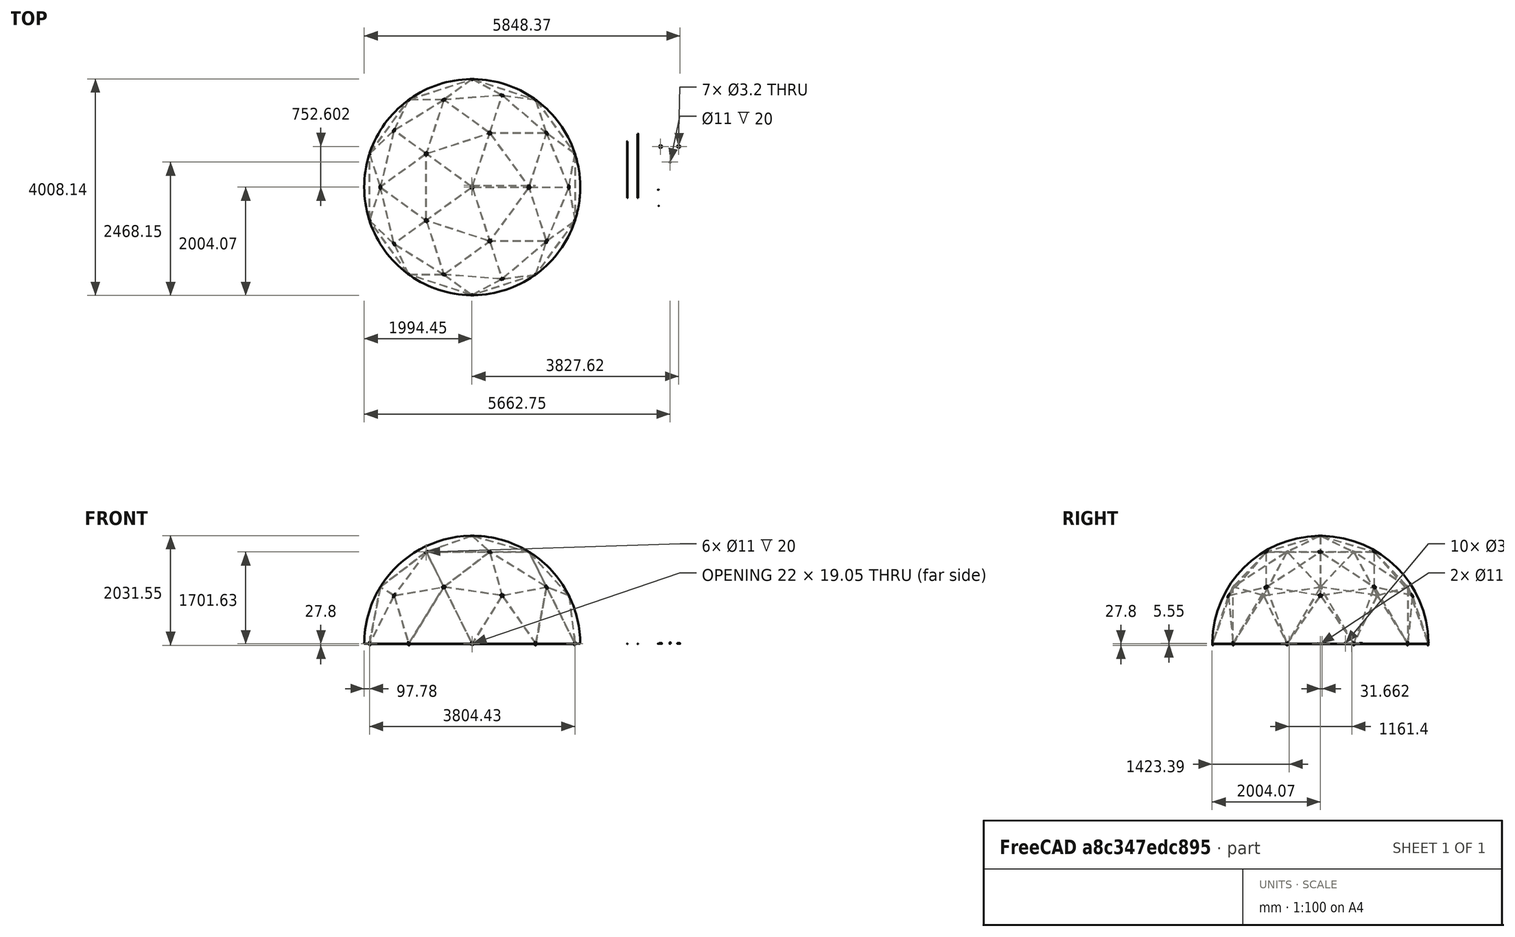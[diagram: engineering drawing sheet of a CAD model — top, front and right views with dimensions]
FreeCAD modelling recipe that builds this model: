
FCSTD DOCUMENT  (FreeCAD 0.16R6707 (Git))
Label: domo-3D
License: All rights reserved
LicenseURL: http://en.wikipedia.org/wiki/All_rights_reserved
objects: Part::Feature×235, Part::Part2DObjectPython×141, App::DocumentObjectGroup×21, App::Annotation×18, Part::Mirroring×7, App::FeaturePython×4, Part::Sphere×1, Part::Cylinder×1
note: 385 computed .brp shape members not serialized (recipe doc carries the construction recipe); baked Part::Feature solids carry a one-line shape summary decoded from their .brp

FEATURE [Part::Part2DObjectPython] Line  # Draft 2D object (typed FeaturePython)
  ChamferSize = 0
  Closed = false
  End = (-1902.16,617.998,0)
  FilletRadius = 0
  Length = 1236.1
  MakeFace = true
  Placement = pos=(-1154.86,1595.54,0) rot=(0,0,-1;0.628319rad)
  Points = (2) [(-30,6,0),(-30,-1230.1,0)]
  Start = (-1175.6,1618.02,0)
  Subdivisions = 0
FEATURE [Part::Part2DObjectPython] Line003  # Draft 2D object (typed FeaturePython)
  ChamferSize = 0
  Closed = false
  End = (-1175.6,1618.02,0)
  FilletRadius = 0
  Length = 1236.1
  MakeFace = true
  Placement = pos=(3.56417,1969.61,0) rot=(0,0,-1;1.25664rad)
  Points = (2) [(-30,6,0),(-30,-1230.1,0)]
  Start = (3.6e-11,2000,0)
  Subdivisions = 0
FEATURE [Part::Mirroring] Part__Mirroring  label="Line (Mirror #1)"
  Base = (0,0,0)
  Normal = (1,0,0)
  Source = -> Line
FEATURE [Part::Mirroring] Part__Mirroring001  label="Line003 (Mirror #2)"
  Base = (0,0,0)
  Normal = (1,0,0)
  Source = -> Line003
FEATURE [Part::Mirroring] Part__Mirroring002  label="Line (Mirror #3)"
  Base = (0,0,0)
  Normal = (0,1,0)
  Source = -> Line
FEATURE [Part::Mirroring] Part__Mirroring003  label="Line003 (Mirror #4)"
  Base = (0,0,0)
  Normal = (0,1,0)
  Source = -> Line003
FEATURE [Part::Mirroring] Part__Mirroring004  label="Line (Mirror #5)"
  Base = (0,0,0)
  Normal = (0,1,0)
  Source = -> Part__Mirroring
FEATURE [Part::Mirroring] Part__Mirroring005  label="Line003 (Mirror #6)"
  Base = (0,0,0)
  Normal = (0,1,0)
  Source = -> Part__Mirroring001
FEATURE [Part::Part2DObjectPython] Line006  # Draft 2D object (typed FeaturePython)
  ChamferSize = 0
  Closed = false
  End = (-1902.16,-617.998,0)
  FilletRadius = 0
  Length = 1236
  MakeFace = true
  Points = (2) [(-1902.16,617.998,0),(-1902.16,-617.998,0)]
  Start = (-1902.16,617.998,0)
  Subdivisions = 0
FEATURE [Part::Sphere] Sphere
  Angle1 = 0
  Angle2 = 90
  Angle3 = 360
  Radius = 2000
FEATURE [Part::Part2DObjectPython] Line014  # Draft 2D object (typed FeaturePython)
  ChamferSize = 0
  Closed = false
  End = (1902.16,3e-10,0)
  FilletRadius = 0
  Length = 1902.16
  MakeFace = true
  Points = (2) [(-1.99975e-10,3.00133e-10,0),(1902.16,3.0025e-10,0)]
  Start = (0,0,0)
  Subdivisions = 0
FEATURE [Part::Part2DObjectPython] Line015  # Draft 2D object (typed FeaturePython)
  ChamferSize = 0
  Closed = false
  End = (1902.16,3e-10,0)
  FilletRadius = 0
  Length = 1902.16
  MakeFace = true
  Points = (2) [(-1.99975e-10,3.00133e-10,0),(1902.16,3.0025e-10,0)]
  Start = (0,0,0)
  Subdivisions = 0
FEATURE [Part::Part2DObjectPython] Line016  # Draft 2D object (typed FeaturePython)
  ChamferSize = 0
  Closed = false
  End = (587.785,1809.02,0)
  FilletRadius = 0
  Length = 1902.11
  MakeFace = true
  Points = (2) [(-1.99975e-10,3.00133e-10,0),(587.785,1809.02,0)]
  Start = (0,0,0)
  Subdivisions = 0
FEATURE [Part::Part2DObjectPython] Line017  # Draft 2D object (typed FeaturePython)
  ChamferSize = 0
  Closed = false
  End = (-1538.86,1118.05,0)
  FilletRadius = 0
  Length = 1902.13
  MakeFace = true
  Points = (2) [(-1.99975e-10,3.00133e-10,0),(-1538.86,1118.05,0)]
  Start = (0,0,0)
  Subdivisions = 0
FEATURE [Part::Part2DObjectPython] Line018  # Draft 2D object (typed FeaturePython)
  ChamferSize = 0
  Closed = false
  End = (-1538.86,-1118.05,0)
  FilletRadius = 0
  Length = 1902.13
  MakeFace = true
  Points = (2) [(-1.99975e-10,3.00133e-10,0),(-1538.86,-1118.05,0)]
  Start = (0,0,0)
  Subdivisions = 0
FEATURE [Part::Part2DObjectPython] Line019  # Draft 2D object (typed FeaturePython)
  ChamferSize = 0
  Closed = false
  End = (-577.454,-703.099,0)
  FilletRadius = 0
  Length = 1093.1
  MakeFace = true
  Placement = pos=(1075.61,-2380.95,0) rot=(0,0,-1;0.581932rad)
  Points = (2) [(-2300,-600,0),(-2303.19,493.095,0)]
  Start = (-1175.6,-1618.02,0)
  Subdivisions = 0
FEATURE [Part::Part2DObjectPython] Line022  # Draft 2D object (typed FeaturePython)
  ChamferSize = 0
  Closed = false
  End = (587.8,-1809.01,0)
  FilletRadius = 0
  Length = 1902.11
  MakeFace = true
  Points = (2) [(-1.99975e-10,3.00133e-10,0),(587.8,-1809.01,0)]
  Start = (0,0,0)
  Subdivisions = 0
FEATURE [Part::Part2DObjectPython] Line023  # Draft 2D object (typed FeaturePython)
  ChamferSize = 0
  Closed = false
  End = (0,0,2000)
  FilletRadius = 0
  Length = 2000
  MakeFace = true
  Points = (2) [(-1.99975e-10,3.00133e-10,0),(1.22465e-13,-2.99952e-29,2000)]
  Start = (0,0,0)
  Subdivisions = 0
FEATURE [Part::Part2DObjectPython] DWire001  # Draft 2D object (typed FeaturePython)
  ChamferSize = 0
  Closed = true
  End = (1902.16,617.998,0)
  FilletRadius = 0
  Length = 3422.2
  MakeFace = true
  Points = (3) [(1902.16,-617.998,0),(1788.83,-9.64734e-10,894.484),(1902.16,617.998,0)]
  Start = (1902.16,-617.998,0)
  Subdivisions = 0
FEATURE [Part::Part2DObjectPython] DWire  # Draft 2D object (typed FeaturePython)
  ChamferSize = 0
  Closed = true
  End = (587.785,1809.02,0)
  FilletRadius = 0
  Length = 6662.19
  MakeFace = true
  Points = (3) [(1.22465e-13,0,2000),(-1.99975e-10,3.00133e-10,0),(587.785,1809.02,0)]
  Start = (0,0,2000)
  Subdivisions = 0
FEATURE [Part::Mirroring] Part__Mirroring006  label="DWire003 (Mirror #7)"
  Base = (0,0,0)
  Normal = (0,1,0)
FEATURE [Part::Part2DObjectPython] Arc  # Draft 2D object (typed FeaturePython)
  FirstAngle = 56.8247
  LastAngle = 105.817
  MakeFace = true
  Placement = pos=(-1175.6,-1618.02,0) rot=(0,0,1;0rad)
  Radius = 1093.1
FEATURE [Part::Part2DObjectPython] Line026  # Draft 2D object (typed FeaturePython)
  ChamferSize = 0
  Closed = false
  End = (-1902.16,-617.998,0)
  FilletRadius = 0
  Length = 1093.15
  MakeFace = true
  Points = (2) [(-809.424,-588.081,0),(-1902.16,-617.998,0)]
  Start = (-809.424,-588.081,0)
  Subdivisions = 0
FEATURE [Part::Part2DObjectPython] DWire004  # Draft 2D object (typed FeaturePython)
  ChamferSize = 0
  Closed = true
  End = (-1538.86,-1118.05,0)
  FilletRadius = 0
  Length = 6662.22
  MakeFace = true
  Points = (3) [(1.22465e-13,0,2000),(-1.99975e-10,3.00133e-10,0),(-1538.86,-1118.05,0)]
  Start = (0,0,2000)
  Subdivisions = 0
FEATURE [Part::Part2DObjectPython] DWire005  # Draft 2D object (typed FeaturePython)
  ChamferSize = 0
  Closed = true
  End = (-1175.6,-1618.02,0)
  FilletRadius = 0
  Length = 3422.35
  MakeFace = true
  Points = (3) [(-1902.16,-617.998,0),(-1447.19,-1051.45,894.481),(-1175.6,-1618.02,0)]
  Start = (-1902.16,-617.998,0)
  Subdivisions = 0
FEATURE [Part::Part2DObjectPython] Line027  # Draft 2D object (typed FeaturePython)
  ChamferSize = 0
  Closed = false
  End = (-878.683,234.127,0)
  FilletRadius = 0
  Length = 1093.1
  MakeFace = true
  Placement = pos=(-2154.97,-1745.49,0) rot=(0,0,-1;1.93254rad)
  Points = (2) [(-2300,-600,0),(-2303.19,493.095,0)]
  Start = (-1902.16,617.998,0)
  Subdivisions = 0
FEATURE [Part::Part2DObjectPython] Arc003  # Draft 2D object (typed FeaturePython)
  FirstAngle = -20.5593
  LastAngle = 28.7005
  MakeFace = true
  Placement = pos=(-1902.16,617.998,0) rot=(0,0,1;0rad)
  Radius = 1093.1
FEATURE [Part::Part2DObjectPython] DWire006  # Draft 2D object (typed FeaturePython)
  ChamferSize = 0
  Closed = true
  End = (-1538.86,1118.05,0)
  FilletRadius = 0
  Length = 6662.22
  MakeFace = true
  Points = (3) [(1.22465e-13,0,2000),(-1.99975e-10,3.00133e-10,0),(-1538.86,1118.05,0)]
  Start = (0,0,2000)
  Subdivisions = 0
FEATURE [Part::Part2DObjectPython] DWire007  # Draft 2D object (typed FeaturePython)
  ChamferSize = 0
  Closed = true
  End = (-1902.16,617.998,0)
  FilletRadius = 0
  Length = 3422.25
  MakeFace = true
  Points = (3) [(-1175.6,1618.02,0),(-1447.21,1051.46,894.426),(-1902.16,617.998,0)]
  Start = (-1175.6,1618.02,0)
  Subdivisions = 0
FEATURE [Part::Part2DObjectPython] DWire008  # Draft 2D object (typed FeaturePython)
  ChamferSize = 0
  Closed = true
  End = (324.937,-1000.03,1701.28)
  FilletRadius = 0
  Length = 3422.31
  MakeFace = true
  Points = (3) [(2.23523e-10,2.82703e-10,2000),(-850.675,-618.052,1701.28),(324.937,-1000.03,1701.28)]
  Start = (2.24e-10,2.83e-10,2000)
  Subdivisions = 0
FEATURE [Part::Part2DObjectPython] DWire009  # Draft 2D object (typed FeaturePython)
  ChamferSize = 0
  Closed = true
  End = (-2e-10,3e-10,2000)
  FilletRadius = 0
  Length = 3422.3
  MakeFace = true
  Points = (3) [(324.937,-1000.03,1701.28),(1051.49,1.3321e-09,1701.28),(-1.99876e-10,3.00061e-10,2000)]
  Start = (324.937,-1000.03,1701.28)
  Subdivisions = 0
FEATURE [Part::Part2DObjectPython] DWire010  # Draft 2D object (typed FeaturePython)
  ChamferSize = 0
  Closed = true
  End = (324.929,1000.03,1701.28)
  FilletRadius = 0
  Length = 3422.3
  MakeFace = true
  Points = (3) [(-1.99876e-10,3.00061e-10,2000),(1051.49,1.3321e-09,1701.28),(324.929,1000.03,1701.28)]
  Start = (-2e-10,3e-10,2000)
  Subdivisions = 0
FEATURE [Part::Part2DObjectPython] DWire011  # Draft 2D object (typed FeaturePython)
  ChamferSize = 0
  Closed = true
  End = (-850.675,618.052,1701.28)
  FilletRadius = 0
  Length = 3422.3
  MakeFace = true
  Points = (3) [(-1.99876e-10,3.00061e-10,2000),(324.929,1000.03,1701.28),(-850.675,618.052,1701.28)]
  Start = (-2e-10,3e-10,2000)
  Subdivisions = 0
FEATURE [Part::Part2DObjectPython] DWire012  # Draft 2D object (typed FeaturePython)
  ChamferSize = 0
  Closed = true
  End = (-850.675,-618.052,1701.28)
  FilletRadius = 0
  Length = 3422.3
  MakeFace = true
  Points = (3) [(-1.99876e-10,3.00061e-10,2000),(-850.675,618.052,1701.28),(-850.675,-618.052,1701.28)]
  Start = (-2e-10,3e-10,2000)
  Subdivisions = 0
FEATURE [Part::Part2DObjectPython] Line040  # Draft 2D object (typed FeaturePython)
  ChamferSize = 0
  Closed = false
  End = (-1447.19,-1051.45,894.481)
  FilletRadius = 0
  Length = 1092.97
  MakeFace = true
  Points = (2) [(-850.675,-618.052,1701.28),(-1447.19,-1051.45,894.481)]
  Start = (-850.675,-618.052,1701.28)
  Subdivisions = 0
FEATURE [Part::Part2DObjectPython] DWire013  # Draft 2D object (typed FeaturePython)
  ChamferSize = 0
  Closed = true
  End = (0,0,2000)
  FilletRadius = 0
  Length = 6662.22
  MakeFace = true
  Points = (3) [(1538.88,-1118.01,0),(-1.99975e-10,3.00133e-10,0),(1.22465e-13,0,2000)]
  Start = (1538.88,-1118.01,0)
  Subdivisions = 0
FEATURE [Part::Part2DObjectPython] Arc007  # Draft 2D object (typed FeaturePython)
  FirstAngle = -90
  LastAngle = 6.05971
  MakeFace = true
  Placement = pos=(-2e-10,3e-10,0) rot=(-0.908667,0.295233,-0.295233;1.66643rad)
  Radius = 2000
  Support = -> DWire013
FEATURE [Part::Part2DObjectPython] DWire014  # Draft 2D object (typed FeaturePython)
  ChamferSize = 0
  Closed = true
  End = (1902.16,-617.998,0)
  FilletRadius = 0
  Length = 3708.32
  MakeFace = true
  Points = (3) [(1175.6,-1618.02,0),(1376.39,-999.957,1051.5),(1902.16,-617.998,0)]
  Start = (1175.6,-1618.02,0)
  Subdivisions = 0
FEATURE [Part::Part2DObjectPython] DWire015  # Draft 2D object (typed FeaturePython)
  ChamferSize = 0
  Closed = true
  End = (1051.49,1.332e-09,1701.28)
  FilletRadius = 0
  Length = 3708.12
  MakeFace = true
  Points = (3) [(1376.39,-999.957,1051.5),(324.937,-1000.03,1701.28),(1051.49,1.3321e-09,1701.28)]
  Start = (1376.39,-999.957,1051.5)
  Subdivisions = 0
FEATURE [Part::Part2DObjectPython] DWire016  # Draft 2D object (typed FeaturePython)
  ChamferSize = 0
  Closed = true
  End = (1175.6,-1618.02,0)
  FilletRadius = 0
  Length = 3422.29
  MakeFace = true
  Points = (3) [(552.796,-1701.28,894.456),(1376.39,-999.957,1051.5),(1175.6,-1618.02,0)]
  Start = (552.796,-1701.28,894.456)
  Subdivisions = 0
FEATURE [Part::Part2DObjectPython] DWire017  # Draft 2D object (typed FeaturePython)
  ChamferSize = 0
  Closed = true
  End = (1902.16,-617.998,0)
  FilletRadius = 0
  Length = 3422.23
  MakeFace = true
  Points = (3) [(1376.39,-999.957,1051.5),(1788.83,-9.64734e-10,894.484),(1902.16,-617.998,0)]
  Start = (1376.39,-999.957,1051.5)
  Subdivisions = 0
FEATURE [Part::Part2DObjectPython] DWire018  # Draft 2D object (typed FeaturePython)
  ChamferSize = 0
  Closed = true
  End = (1376.39,-999.957,1051.5)
  FilletRadius = 0
  Length = 3422.11
  MakeFace = true
  Points = (3) [(324.937,-1000.03,1701.28),(552.796,-1701.28,894.456),(1376.39,-999.957,1051.5)]
  Start = (324.937,-1000.03,1701.28)
  Subdivisions = 0
FEATURE [Part::Part2DObjectPython] DWire019  # Draft 2D object (typed FeaturePython)
  ChamferSize = 0
  Closed = true
  End = (1788.83,-9.65e-10,894.484)
  FilletRadius = 0
  Length = 3421.98
  MakeFace = true
  Points = (3) [(1376.39,-999.957,1051.5),(1051.49,1.3321e-09,1701.28),(1788.83,-9.64734e-10,894.484)]
  Start = (1376.39,-999.957,1051.5)
  Subdivisions = 0
FEATURE [Part::Part2DObjectPython] DWire020  # Draft 2D object (typed FeaturePython)
  ChamferSize = 0
  Closed = true
  End = (1175.6,1618.02,0)
  FilletRadius = 0
  Length = 3708.32
  MakeFace = true
  Points = (3) [(1902.16,617.998,0),(1376.39,999.957,1051.5),(1175.6,1618.02,0)]
  Start = (1902.16,617.998,0)
  Subdivisions = 0
FEATURE [Part::Part2DObjectPython] DWire021  # Draft 2D object (typed FeaturePython)
  ChamferSize = 0
  Closed = true
  End = (-1175.6,1618.02,0)
  FilletRadius = 0
  Length = 3708.32
  MakeFace = true
  Points = (3) [(-525.738,1618.01,1051.5),(3.56977e-11,2000,0),(-1175.6,1618.02,0)]
  Start = (-525.738,1618.01,1051.5)
  Subdivisions = 0
FEATURE [Part::Part2DObjectPython] DWire022  # Draft 2D object (typed FeaturePython)
  ChamferSize = 0
  Closed = true
  End = (-1902.16,-617.998,0)
  FilletRadius = 0
  Length = 3708.18
  MakeFace = true
  Points = (3) [(-1701.28,-1.02242e-09,1051.5),(-1902.16,617.998,0),(-1902.16,-617.998,0)]
  Start = (-1701.28,-1.022e-09,1051.5)
  Subdivisions = 0
FEATURE [Part::Part2DObjectPython] DWire023  # Draft 2D object (typed FeaturePython)
  ChamferSize = 0
  Closed = true
  End = (-3.6e-11,-2000,0)
  FilletRadius = 0
  Length = 3708.32
  MakeFace = true
  Points = (3) [(-525.738,-1618.01,1051.5),(-1175.6,-1618.02,0),(-3.5925e-11,-2000,0)]
  Start = (-525.738,-1618.01,1051.5)
  Subdivisions = 0
FEATURE [Part::Part2DObjectPython] DWire024  # Draft 2D object (typed FeaturePython)
  ChamferSize = 0
  Closed = true
  End = (324.929,1000.03,1701.28)
  FilletRadius = 0
  Length = 3708.14
  MakeFace = true
  Points = (3) [(1051.49,1.3321e-09,1701.28),(1376.39,999.957,1051.5),(324.929,1000.03,1701.28)]
  Start = (1051.49,1.332e-09,1701.28)
  Subdivisions = 0
FEATURE [Part::Part2DObjectPython] DWire025  # Draft 2D object (typed FeaturePython)
  ChamferSize = 0
  Closed = true
  End = (1376.39,999.957,1051.5)
  FilletRadius = 0
  Length = 3421.98
  MakeFace = true
  Points = (3) [(1051.49,1.3321e-09,1701.28),(1788.83,-9.64734e-10,894.484),(1376.39,999.957,1051.5)]
  Start = (1051.49,1.332e-09,1701.28)
  Subdivisions = 0
FEATURE [Part::Part2DObjectPython] DWire026  # Draft 2D object (typed FeaturePython)
  ChamferSize = 0
  Closed = true
  End = (1376.39,999.957,1051.5)
  FilletRadius = 0
  Length = 3422.23
  MakeFace = true
  Points = (3) [(1788.83,-9.64734e-10,894.484),(1902.16,617.998,0),(1376.39,999.957,1051.5)]
  Start = (1788.83,-9.65e-10,894.484)
  Subdivisions = 0
FEATURE [Part::Part2DObjectPython] DWire027  # Draft 2D object (typed FeaturePython)
  ChamferSize = 0
  Closed = true
  End = (552.796,1701.28,894.456)
  FilletRadius = 0
  Length = 3422.29
  MakeFace = true
  Points = (3) [(1376.39,999.957,1051.5),(1175.6,1618.02,0),(552.796,1701.28,894.456)]
  Start = (1376.39,999.957,1051.5)
  Subdivisions = 0
FEATURE [Part::Part2DObjectPython] DWire028  # Draft 2D object (typed FeaturePython)
  ChamferSize = 0
  Closed = true
  End = (552.796,1701.28,894.456)
  FilletRadius = 0
  Length = 3422.12
  MakeFace = true
  Points = (3) [(324.929,1000.03,1701.28),(1376.39,999.957,1051.5),(552.796,1701.28,894.456)]
  Start = (324.929,1000.03,1701.28)
  Subdivisions = 0
FEATURE [Part::Part2DObjectPython] DWire029  # Draft 2D object (typed FeaturePython)
  ChamferSize = 0
  Closed = true
  End = (-3.6e-11,2000,0)
  FilletRadius = 0
  Length = 3422.29
  MakeFace = true
  Points = (3) [(-525.738,1618.01,1051.5),(552.796,1701.28,894.456),(-3.5925e-11,2000,0)]
  Start = (-525.738,1618.01,1051.5)
  Subdivisions = 0
FEATURE [Part::Part2DObjectPython] DWire030  # Draft 2D object (typed FeaturePython)
  ChamferSize = 0
  Closed = true
  End = (-525.738,1618.01,1051.5)
  FilletRadius = 0
  Length = 3422.11
  MakeFace = true
  Points = (3) [(324.929,1000.03,1701.28),(552.796,1701.28,894.456),(-525.738,1618.01,1051.5)]
  Start = (324.929,1000.03,1701.28)
  Subdivisions = 0
FEATURE [Part::Part2DObjectPython] DWire031  # Draft 2D object (typed FeaturePython)
  ChamferSize = 0
  Closed = true
  End = (-850.675,618.052,1701.28)
  FilletRadius = 0
  Length = 3708.14
  MakeFace = true
  Points = (3) [(324.929,1000.03,1701.28),(-525.738,1618.01,1051.5),(-850.675,618.052,1701.28)]
  Start = (324.929,1000.03,1701.28)
  Subdivisions = 0
FEATURE [Part::Part2DObjectPython] DWire032  # Draft 2D object (typed FeaturePython)
  ChamferSize = 0
  Closed = true
  End = (-1447.21,1051.46,894.426)
  FilletRadius = 0
  Length = 3422.21
  MakeFace = true
  Points = (3) [(-525.738,1618.01,1051.5),(-1175.6,1618.02,0),(-1447.21,1051.46,894.426)]
  Start = (-525.738,1618.01,1051.5)
  Subdivisions = 0
FEATURE [Part::Part2DObjectPython] DWire033  # Draft 2D object (typed FeaturePython)
  ChamferSize = 0
  Closed = true
  End = (-1447.21,1051.46,894.426)
  FilletRadius = 0
  Length = 3422.1
  MakeFace = true
  Points = (3) [(-525.738,1618.01,1051.5),(-850.675,618.052,1701.28),(-1447.21,1051.46,894.426)]
  Start = (-525.738,1618.01,1051.5)
  Subdivisions = 0
FEATURE [Part::Part2DObjectPython] DWire034  # Draft 2D object (typed FeaturePython)
  ChamferSize = 0
  Closed = true
  End = (-1701.28,-1.022e-09,1051.5)
  FilletRadius = 0
  Length = 3422.12
  MakeFace = true
  Points = (3) [(-850.675,618.052,1701.28),(-1447.21,1051.46,894.426),(-1701.28,-1.02242e-09,1051.5)]
  Start = (-850.675,618.052,1701.28)
  Subdivisions = 0
FEATURE [Part::Part2DObjectPython] DWire035  # Draft 2D object (typed FeaturePython)
  ChamferSize = 0
  Closed = true
  End = (-1701.28,-1.022e-09,1051.5)
  FilletRadius = 0
  Length = 3422.26
  MakeFace = true
  Points = (3) [(-1447.21,1051.46,894.426),(-1902.16,617.998,0),(-1701.28,-1.02242e-09,1051.5)]
  Start = (-1447.21,1051.46,894.426)
  Subdivisions = 0
FEATURE [Part::Part2DObjectPython] DWire036  # Draft 2D object (typed FeaturePython)
  ChamferSize = 0
  Closed = true
  End = (-850.675,-618.052,1701.28)
  FilletRadius = 0
  Length = 3708.14
  MakeFace = true
  Points = (3) [(-850.675,618.052,1701.28),(-1701.28,-1.02242e-09,1051.5),(-850.675,-618.052,1701.28)]
  Start = (-850.675,618.052,1701.28)
  Subdivisions = 0
FEATURE [Part::Part2DObjectPython] DWire037  # Draft 2D object (typed FeaturePython)
  ChamferSize = 0
  Closed = true
  End = (-1447.19,-1051.45,894.481)
  FilletRadius = 0
  Length = 3422.04
  MakeFace = true
  Points = (3) [(-1701.28,-1.02242e-09,1051.5),(-850.675,-618.052,1701.28),(-1447.19,-1051.45,894.481)]
  Start = (-1701.28,-1.022e-09,1051.5)
  Subdivisions = 0
FEATURE [Part::Part2DObjectPython] DWire038  # Draft 2D object (typed FeaturePython)
  ChamferSize = 0
  Closed = true
  End = (-1447.19,-1051.45,894.481)
  FilletRadius = 0
  Length = 3422.29
  MakeFace = true
  Points = (3) [(-1701.28,-1.02242e-09,1051.5),(-1902.16,-617.998,0),(-1447.19,-1051.45,894.481)]
  Start = (-1701.28,-1.022e-09,1051.5)
  Subdivisions = 0
FEATURE [Part::Part2DObjectPython] DWire039  # Draft 2D object (typed FeaturePython)
  ChamferSize = 0
  Closed = true
  End = (-525.738,-1618.01,1051.5)
  FilletRadius = 0
  Length = 3422.02
  MakeFace = true
  Points = (3) [(-850.675,-618.052,1701.28),(-1447.19,-1051.45,894.481),(-525.738,-1618.01,1051.5)]
  Start = (-850.675,-618.052,1701.28)
  Subdivisions = 0
FEATURE [Part::Part2DObjectPython] DWire040  # Draft 2D object (typed FeaturePython)
  ChamferSize = 0
  Closed = true
  End = (324.937,-1000.03,1701.28)
  FilletRadius = 0
  Length = 3708.15
  MakeFace = true
  Points = (3) [(-850.675,-618.052,1701.28),(-525.738,-1618.01,1051.5),(324.937,-1000.03,1701.28)]
  Start = (-850.675,-618.052,1701.28)
  Subdivisions = 0
FEATURE [Part::Part2DObjectPython] DWire041  # Draft 2D object (typed FeaturePython)
  ChamferSize = 0
  Closed = true
  End = (-1447.19,-1051.45,894.481)
  FilletRadius = 0
  Length = 3422.24
  MakeFace = true
  Points = (3) [(-525.738,-1618.01,1051.5),(-1175.6,-1618.02,0),(-1447.19,-1051.45,894.481)]
  Start = (-525.738,-1618.01,1051.5)
  Subdivisions = 0
FEATURE [Part::Part2DObjectPython] DWire042  # Draft 2D object (typed FeaturePython)
  ChamferSize = 0
  Closed = true
  End = (552.796,-1701.28,894.456)
  FilletRadius = 0
  Length = 3422.12
  MakeFace = true
  Points = (3) [(-525.738,-1618.01,1051.5),(324.937,-1000.03,1701.28),(552.796,-1701.28,894.456)]
  Start = (-525.738,-1618.01,1051.5)
  Subdivisions = 0
FEATURE [Part::Part2DObjectPython] DWire043  # Draft 2D object (typed FeaturePython)
  ChamferSize = 0
  Closed = true
  End = (552.796,-1701.28,894.456)
  FilletRadius = 0
  Length = 3422.29
  MakeFace = true
  Points = (3) [(-525.738,-1618.01,1051.5),(-3.5925e-11,-2000,0),(552.796,-1701.28,894.456)]
  Start = (-525.738,-1618.01,1051.5)
  Subdivisions = 0
FEATURE [App::DocumentObjectGroup] Group001  label="Top-pentagon"
  Group = -> [DWire010,DWire011,DWire012,DWire008,DWire009]
FEATURE [App::DocumentObjectGroup] Group002  label="Pentagon-1"
  Group = -> [DWire019,DWire025,DWire026,DWire001,DWire017]
FEATURE [App::DocumentObjectGroup] Group003  label="Pentagon-2"
  Group = -> [DWire028,DWire030,DWire029,Part__Mirroring006,DWire027]
FEATURE [App::DocumentObjectGroup] Group004  label="Pentagon-3"
  Group = -> [DWire033,DWire034,DWire035,DWire007,DWire032]
FEATURE [App::DocumentObjectGroup] Group005  label="Pentagon-4"
  Group = -> [DWire037,DWire038,DWire005,DWire041,Line040,DWire039]
FEATURE [Part::Part2DObjectPython] DWire044  # Draft 2D object (typed FeaturePython)
  ChamferSize = 0
  Closed = true
  End = (1175.6,-1618.02,0)
  FilletRadius = 0
  Length = 3422.3
  MakeFace = true
  Points = (3) [(-3.5925e-11,-2000,0),(552.796,-1701.28,894.456),(1175.6,-1618.02,0)]
  Start = (-3.6e-11,-2000,0)
  Subdivisions = 0
FEATURE [App::DocumentObjectGroup] Group006  label="Pentagon-5"
  Group = -> [DWire042,DWire043,DWire016,DWire018,DWire044]
FEATURE [App::DocumentObjectGroup] Group007  label="Aux"
  Group = -> [Part__Mirroring002,Part__Mirroring003,Part__Mirroring004,Part__Mirroring005,Line006,Line014,Line015,Line016,Line017,Line018,Line019,Line022,Line023,DWire,Arc,Line026,DWire004,Line027,Arc003,DWire006,DWire013,Arc007,Sphere]
FEATURE [Part::Part2DObjectPython] DWire045  label="Bottom"  # Draft 2D object (typed FeaturePython)
  ChamferSize = 0
  Closed = true
  End = (1902.16,-617.998,0)
  FilletRadius = 0
  Length = 12360.8
  MakeFace = true
  Points = (10) [(1902.16,617.998,0),(1175.6,1618.02,0),(3.56977e-11,2000,0),(-1175.6,1618.02,0),(-1902.16,617.998,0),(-1902.16,-617.998,0),(-1175.6,-1618.02,0),+3 more]
  Start = (1902.16,617.998,0)
  Subdivisions = 0
FEATURE [App::DocumentObjectGroup] Group008  label="Green-triangles"
  Group = -> [DWire023,DWire040,DWire015,DWire014,DWire024,DWire031,DWire036,DWire022,DWire021,DWire020]
FEATURE [Part::Feature] Clone002  label="Hub-007"
  Placement = pos=(1044.95,2.83e-10,1690.69) rot=(0.191324,0.71403,0.673466;0.757331rad)
  shape: bbox 49.68 x 55.6 x 37.22 mm, 28 faces (baked)
FEATURE [Part::Feature] Clone005  label="strutcap004"
  Placement = pos=(1066.92,2.83e-10,1684.4) rot=(0.932253,0,0.361806;3.14159rad)
  shape: bbox 31.1 x 20 x 29.82 mm, 19 faces (baked)
FEATURE [Part::Feature] Clone008  label="strutcap007"
  Placement = pos=(1038.85,-19.0526,1701.75) rot=(0.667656,-0.64473,0.372235;1.42598rad)
  shape: bbox 25.29 x 31.07 x 25.73 mm, 19 faces (baked)
FEATURE [Part::Feature] Clone009  label="strutcap008"
  Placement = pos=(1029.49,2.83e-10,1707.53) rot=(0,-1,0;1.294rad)
  shape: bbox 31.29 x 20 x 25.37 mm, 19 faces (baked)
FEATURE [Part::Feature] Clone028  label="strutcap025"
  Placement = pos=(1902.2,-594.877,0) rot=(-1,-1.4e-05,1.4e-05;1.5708rad)
  shape: bbox 20.3 x 30 x 20 mm, 19 faces (baked)
FEATURE [Part::Feature] Clone030  label="strutcap027"
  Placement = pos=(1888.76,-636.496,0) rot=(0.909046,-0.294649,-0.294649;1.66601rad)
  shape: bbox 27.81 x 32.24 x 20 mm, 19 faces (baked)
FEATURE [Part::Feature] Clone031  label="Hub-012"
  Placement = pos=(1889.5,-613.884,0) rot=(0.154555,0.97582,-0.154555;1.59527rad)
  shape: bbox 27.47 x 52.09 x 55.6 mm, 28 faces (baked)
FEATURE [Part::Feature] Cylinder014  label="Varilla-B-modif-003"
  Placement = pos=(1902.16,593.953,0) rot=(1,1.4e-05,1.4e-05;1.5708rad)
  shape: bbox 10.03 x 1189 x 10 mm, 3 faces (baked)
FEATURE [App::DocumentObjectGroup] Group012
FEATURE [App::DocumentObjectGroup] Group  label="Domo-superficies"
  Group = -> [Group001,Group002,Group003,Group004,Group005,Group006,Group008,DWire045,Group012]
FEATURE [Part::Feature] Clone001004  label="Hub5-01-clave002"
  Placement = pos=(-1.81309e-05,2.83e-10,1987.55) rot=(0,0,-1;0.314151rad)
  shape: bbox 54.38 x 55.6 x 12.4 mm, 25 faces (baked)
FEATURE [Part::Feature] Clone  label="strutcap031"
  Placement = pos=(22.0001,2.83e-10,1993.75) rot=(0.797896,0,0.602796;3.14159rad)
  shape: bbox 32.05 x 20 x 22.68 mm, 19 faces (baked)
FEATURE [Part::Feature] Clone001005  label="Hub5-01-clave003"
  Placement = pos=(1777.69,2.83e-10,888.915) rot=(0.523905,0.082976,0.847726;2.87466rad)
  shape: bbox 33.84 x 55.6 x 51.33 mm, 25 faces (baked)
FEATURE [Part::Feature] Clone001006  label="strutcap032"
  Placement = pos=(1773.4,2.83e-10,911.365) rot=(0,-1,0;0.740475rad)
  shape: bbox 29.03 x 20 x 31.71 mm, 19 faces (baked)
FEATURE [Part::Feature] Clone001007  label="Hub-014"
  Placement = pos=(1889.5,613.885,0) rot=(-0.154531,0.975828,0.154531;1.59526rad)
  shape: bbox 27.47 x 52.09 x 55.6 mm, 28 faces (baked)
FEATURE [Part::Feature] Clone001008  label="strutcap033"
  Placement = pos=(1902.19,595.158,0) rot=(1,0.00069,0.00069;1.5708rad)
  shape: bbox 20.33 x 30.01 x 20 mm, 19 faces (baked)
FEATURE [Part::Feature] Clone001009  label="strutcap034"
  Placement = pos=(1888.6,636.724,0) rot=(-0.908667,-0.295233,0.295233;1.66643rad)
  shape: bbox 27.82 x 32.23 x 20 mm, 19 faces (baked)
FEATURE [Part::Feature] Clone001010  label="strutcap035"
  Placement = pos=(1899.8,-604.923,18.9221) rot=(-0.98127,-0.136231,0.136202;0.618302rad)
  shape: bbox 20 x 28.03 x 30.96 mm, 19 faces (baked)
FEATURE [Part::Feature] Clone001012  label="strutcap037"
  Placement = pos=(1791.2,-12.9311,875.769) rot=(0.998074,0.043631,0.044104;2.5353rad)
  shape: bbox 22.47 x 27.49 x 30.68 mm, 19 faces (baked)
FEATURE [Part::Cylinder] Cylinder015  label="Cylinder084"
  Angle = 360
  Height = 1047.11
  Placement = pos=(1066.92,2.83e-10,1684.4) rot=(0.681894,-0.681894,0.264655;3.65904rad)
  Radius = 5
FEATURE [Part::Feature] Cylinder016  label="Cylinder001"
  Placement = pos=(1791.23,-12.9283,875.771) rot=(0.998113,0.043415,0.043415;2.53525rad)
  shape: bbox 118.5 x 600.2 x 862.6 mm, 3 faces (baked)
FEATURE [Part::Feature] Clone001013  label="strutcap038"
  Placement = pos=(1791.12,13.8918,876.408) rot=(0.993179,0.082001,0.082896;3.73273rad)
  shape: bbox 22.73 x 28.03 x 30.67 mm, 19 faces (baked)
FEATURE [Part::Feature] Cylinder017  label="Cylinder002"
  Placement = pos=(1791.15,13.8946,876.414) rot=(0.993219,0.08221,0.08221;3.73262rad)
  shape: bbox 118.5 x 600.7 x 862.3 mm, 3 faces (baked)
FEATURE [Part::Feature] Clone001014  label="strutcap039"
  Placement = pos=(1899.68,606.357,19.8831) rot=(0.934186,-0.252314,0.25226;0.634069rad)
  shape: bbox 20 x 27.5 x 31.62 mm, 19 faces (baked)
FEATURE [Part::Feature] Cylinder018  label="Cylinder003"
  Placement = pos=(22.0001,2.83e-10,1993.75) rot=(-0.623692,0.623692,-0.471188;2.26093rad)
  shape: bbox 1010 x 10 x 295.8 mm, 3 faces (baked)
FEATURE [Part::Feature] Cylinder019  label="Cylinder004"
  Placement = pos=(6.79821,20.9234,1993.75) rot=(-0.980863,0.155349,-0.117363;1.86613rad)
  shape: bbox 320.8 x 962 x 295.8 mm, 3 faces (baked)
FEATURE [Part::Feature] Clone001015  label="strutcap040"
  Placement = pos=(6.79821,20.9234,1993.75) rot=(0.690291,0.501531,0.521503;3.86596rad)
  shape: bbox 23.54 x 32.47 x 22.68 mm, 19 faces (baked)
FEATURE [Part::Feature] Clone001016  label="strutcap041"
  Placement = pos=(318.122,979.108,1707.53) rot=(0.463915,-0.638519,0.614065;1.73821rad)
  shape: bbox 23.11 x 31.33 x 25.37 mm, 19 faces (baked)
FEATURE [Part::Feature] Clone001018  label="Hub-015"
  Placement = pos=(322.898,993.806,1690.69) rot=(-0.123041,0.320528,0.939214;1.84115rad)
  shape: bbox 55.11 x 51.63 x 37.22 mm, 28 faces (baked)
FEATURE [Part::Feature] Clone001020  label="strutcap044"
  Placement = pos=(339.134,982.12,1701.75) rot=(0.773329,-0.182879,0.607056;2.21695rad)
  shape: bbox 29.76 x 30.45 x 20.75 mm, 19 faces (baked)
FEATURE [Part::Feature] Clone007  label="strutcap006"
  Placement = pos=(1038.85,19.0526,1701.75) rot=(-0.64113,-0.730539,-0.235086;1.6431rad)
  shape: bbox 27.52 x 31.98 x 20.74 mm, 19 faces (baked)
FEATURE [Part::Feature] Cylinder020  label="Varilla-B-modif-004"
  Placement = pos=(340.068,980.833,1701.75) rot=(0.90866,0.295244,0.295244;1.66644rad)
  shape: bbox 706.9 x 967.7 x 10 mm, 3 faces (baked)
FEATURE [Part::Part2DObjectPython] Line045  label="h"  # Draft 2D object (typed FeaturePython)
  ChamferSize = 0
  Closed = false
  End = (-2e-10,3e-10,2000)
  FilletRadius = 0
  Length = 2000
  MakeFace = true
  Points = (2) [(-1.99876e-10,3.00061e-10,0),(-1.99876e-10,3.00061e-10,2000)]
  Start = (0,0,0)
  Subdivisions = 0
  Support = -> DWire045
FEATURE [Part::Feature] Clone001023  label="Hub-016"
  Placement = pos=(1367.83,993.738,1044.94) rot=(0.480375,0.156077,0.863064;3.68838rad)
  shape: bbox 46.36 x 51.63 x 50.11 mm, 28 faces (baked)
FEATURE [Part::Feature] Clone001027  label="strutcap049"
  Placement = pos=(1385.02,979.037,1048.2) rot=(0.929901,-0.068235,0.361425;1.8922rad)
  shape: bbox 27.6 x 31.33 x 20.3 mm, 19 faces (baked)
FEATURE [Part::Feature] Clone001030  label="strutcap052"
  Placement = pos=(1779.91,20.6545,898.82) rot=(-0.909103,-0.414228,-0.044114;1.42856rad)
  shape: bbox 24.46 x 32.53 x 22.38 mm, 19 faces (baked)
FEATURE [Part::Feature] Cylinder021  label="Cylinder005"
  Placement = pos=(1779.94,20.6643,898.834) rot=(-0.908834,-0.414887,-0.043473;1.42913rad)
  shape: bbox 403.8 x 962.4 x 159.4 mm, 3 faces (baked)
FEATURE [Part::Feature] Clone001031  label="strutcap053"
  Placement = pos=(1780.84,-21.3342,896.949) rot=(0.871498,-0.474485,0.123916;1.43836rad)
  shape: bbox 24.48 x 32.39 x 22.88 mm, 19 faces (baked)
FEATURE [Part::Feature] Cylinder022  label="Cylinder006"
  Placement = pos=(1780.87,-21.342,896.969) rot=(0.871257,-0.475095,0.123269;1.43902rad)
  shape: bbox 404.7 x 961.7 x 161.3 mm, 3 faces (baked)
FEATURE [Part::Feature] Clone001032  label="strutcap054"
  Placement = pos=(1385.02,-979.035,1048.21) rot=(-0.930319,-0.067054,-0.360569;1.89034rad)
  shape: bbox 27.6 x 31.33 x 20.29 mm, 19 faces (baked)
FEATURE [Part::Feature] Clone001033  label="Hub-017"
  Placement = pos=(1367.82,-993.731,1044.96) rot=(0.270395,0.832171,-0.484126;1.1821rad)
  shape: bbox 46.31 x 51.62 x 50.16 mm, 28 faces (baked)
FEATURE [Part::Feature] Clone001036  label="strutcap057"
  Placement = pos=(1359.16,-1014.63,1048.21) rot=(0.830217,-0.556143,-0.038018;1.57228rad)
  shape: bbox 27.82 x 32.54 x 20 mm, 19 faces (baked)
FEATURE [Part::Feature] Clone001037  label="strutcap058"
  Placement = pos=(1373.71,-1011.61,1031.99) rot=(0.909326,-0.37369,0.182983;2.49398rad)
  shape: bbox 21.91 x 31.15 x 29.81 mm, 19 faces (baked)
FEATURE [Part::Feature] Clone001038  label="strutcap059"
  Placement = pos=(1386.64,-993.808,1031.99) rot=(0.962095,-0.192679,0.192997;3.57034rad)
  shape: bbox 28.43 x 23.66 x 30.86 mm, 19 faces (baked)
FEATURE [Part::Part2DObjectPython] Line054  # Draft 2D object (typed FeaturePython)
  ChamferSize = 0
  Closed = false
  End = (1902.16,-617.998,0)
  FilletRadius = 0
  Length = 1236.1
  MakeFace = true
  Points = (2) [(1175.6,-1618.02,0),(1902.16,-617.998,0)]
  Start = (1175.6,-1618.02,0)
  Subdivisions = 0
FEATURE [Part::Part2DObjectPython] Line055  # Draft 2D object (typed FeaturePython)
  ChamferSize = 0
  Closed = false
  End = (1902.16,617.998,0)
  FilletRadius = 0
  Length = 1236
  MakeFace = true
  Points = (2) [(1902.16,-617.998,0),(1902.16,617.998,0)]
  Start = (1902.16,-617.998,0)
  Subdivisions = 0
FEATURE [Part::Part2DObjectPython] Line056  # Draft 2D object (typed FeaturePython)
  ChamferSize = 0
  Closed = false
  End = (1376.39,-999.957,1051.5)
  FilletRadius = 0
  Length = 1236
  MakeFace = true
  Points = (2) [(1051.49,1.3321e-09,1701.28),(1376.39,-999.957,1051.5)]
  Start = (1051.49,1.332e-09,1701.28)
  Subdivisions = 0
FEATURE [Part::Part2DObjectPython] Line057  # Draft 2D object (typed FeaturePython)
  ChamferSize = 0
  Closed = false
  End = (1902.16,-617.998,0)
  FilletRadius = 0
  Length = 1236.11
  MakeFace = true
  Points = (2) [(1376.39,-999.957,1051.5),(1902.16,-617.998,0)]
  Start = (1376.39,-999.957,1051.5)
  Subdivisions = 0
FEATURE [Part::Part2DObjectPython] Line058  # Draft 2D object (typed FeaturePython)
  ChamferSize = 0
  Closed = false
  End = (1376.39,999.957,1051.5)
  FilletRadius = 0
  Length = 1236
  MakeFace = true
  Points = (2) [(1051.49,1.3321e-09,1701.28),(1376.39,999.957,1051.5)]
  Start = (1051.49,1.332e-09,1701.28)
  Subdivisions = 0
FEATURE [Part::Part2DObjectPython] Line059  # Draft 2D object (typed FeaturePython)
  ChamferSize = 0
  Closed = false
  End = (1902.16,617.998,0)
  FilletRadius = 0
  Length = 1236.11
  MakeFace = true
  Points = (2) [(1376.39,999.957,1051.5),(1902.16,617.998,0)]
  Start = (1376.39,999.957,1051.5)
  Subdivisions = 0
FEATURE [Part::Feature] Cylinder023  label="Varilla-B-modif-005"
  Placement = pos=(1891.94,625.428,20.4541) rot=(-0.256517,-0.683428,-0.683465;0.767356rad)
  shape: bbox 514.7 x 376.8 x 1017 mm, 3 faces (baked)
FEATURE [Part::Feature] Clone001039  label="strutcap060"
  Placement = pos=(1386.87,993.248,1032.31) rot=(0.963511,0.189033,0.189506;2.73838rad)
  shape: bbox 28.28 x 23.32 x 30.96 mm, 19 faces (baked)
FEATURE [Part::Feature] Clone001040  label="strutcap061"
  Placement = pos=(1892,626.262,19.0526) rot=(-0.586671,-0.615427,0.526371;0.557536rad)
  shape: bbox 24.41 x 24.08 x 32.46 mm, 19 faces (baked)
FEATURE [Part::Feature] Clone001041  label="strutcap062"
  Placement = pos=(1370.43,982.035,1064.4) rot=(0.652966,-0.542424,0.528594;1.20781rad)
  shape: bbox 22.88 x 30.45 x 29.86 mm, 19 faces (baked)
FEATURE [Part::Feature] Cylinder024  label="Varilla-B-modif-006"
  Placement = pos=(1057.35,20.059,1689.56) rot=(0.887762,0.32548,0.325486;3.92675rad)
  shape: bbox 322.6 x 967 x 634.3 mm, 3 faces (baked)
FEATURE [Part::Feature] Clone001042  label="strutcap063"
  Placement = pos=(1057.34,19.1988,1690.32) rot=(0.882765,0.34052,0.323687;3.95983rad)
  shape: bbox 24.7 x 32.04 x 26.61 mm, 19 faces (baked)
FEATURE [Part::Feature] Cylinder025  label="Varilla-B-modif-007"
  Placement = pos=(1386.68,-992.502,1030.9) rot=(0.93165,0.256925,0.256939;3.33301rad)
  shape: bbox 514.9 x 375.8 x 1017 mm, 3 faces (baked)
FEATURE [Part::Feature] Clone001043  label="strutcap064"
  Placement = pos=(1892.07,-626.034,19.189) rot=(0.64134,-0.542546,-0.542518;0.709896rad)
  shape: bbox 25.5 x 26.02 x 32.03 mm, 19 faces (baked)
FEATURE [Part::Feature] Clone001044  label="strutcap065"
  Placement = pos=(1370.47,-982.061,1064.43) rot=(-0.67332,-0.525087,-0.520503;1.20241rad)
  shape: bbox 22.54 x 30.53 x 29.82 mm, 19 faces (baked)
FEATURE [Part::Feature] Clone001045  label="strutcap066"
  Placement = pos=(1057.56,-19.0526,1690.18) rot=(0.887841,-0.325204,0.325548;2.35642rad)
  shape: bbox 25.29 x 31.82 x 26.9 mm, 19 faces (baked)
FEATURE [Part::Feature] Cylinder027  label="Varilla-B-modif-009"
  Placement = pos=(1370.47,-982.061,1064.43) rot=(-0.669151,-0.525446,-0.525494;1.2188rad)
  shape: bbox 322.1 x 967.7 x 633.5 mm, 3 faces (baked)
FEATURE [Part::Part2DObjectPython] Line060  # Draft 2D object (typed FeaturePython)
  ChamferSize = 0
  Closed = false
  End = (324.929,1000.03,1701.28)
  FilletRadius = 0
  Length = 1236.1
  MakeFace = true
  Points = (2) [(-850.675,618.052,1701.28),(324.929,1000.03,1701.28)]
  Start = (-850.675,618.052,1701.28)
  Subdivisions = 0
FEATURE [Part::Feature] Clone001047  label="strutcap068"
  Placement = pos=(302.894,993.894,1701.75) rot=(-0.095426,-0.931982,0.349719;1.72702rad)
  shape: bbox 31.97 x 22.84 x 20.72 mm, 19 faces (baked)
FEATURE [Part::Feature] Clone001049  label="strutcap070"
  Placement = pos=(-17.7986,12.9312,1993.75) rot=(-0.300922,-0.926155,-0.227341;1.92055rad)
  shape: bbox 31.35 x 28.31 x 22.68 mm, 19 faces (baked)
FEATURE [Part::Feature] Cylinder  label="Cylinder007"
  Placement = pos=(-17.7986,12.9312,1993.75) rot=(-0.842809,-0.429437,0.324432;2.00762rad)
  shape: bbox 821.2 x 600.3 x 295.8 mm, 3 faces (baked)
FEATURE [Part::Feature] Clone001050  label="Hub-018"
  Placement = pos=(-845.385,614.197,1690.69) rot=(-0.229479,0.149024,0.961837;3.04087rad)
  shape: bbox 52.89 x 52.48 x 37.22 mm, 28 faces (baked)
FEATURE [Part::Feature] Clone001051  label="strutcap071"
  Placement = pos=(-832.882,605.113,1707.53) rot=(0.591556,-0.192206,0.783019;2.64333rad)
  shape: bbox 30.27 x 27.49 x 25.37 mm, 19 faces (baked)
FEATURE [Part::Feature] Clone001052  label="strutcap072"
  Placement = pos=(-829.253,626.027,1701.75) rot=(0.656731,0.274649,0.702334;3.0586rad)
  shape: bbox 31.36 x 25.66 x 20.75 mm, 19 faces (baked)
FEATURE [Part::Feature] Clone001053  label="strutcap073"
  Placement = pos=(-844.393,637.027,1690.18) rot=(0.558841,0.681764,0.472117;3.47389rad)
  shape: bbox 22.99 x 32.33 x 26.68 mm, 19 faces (baked)
FEATURE [Part::Feature] Clone001054  label="strutcap074"
  Placement = pos=(-863.162,627.113,1684.4) rot=(0.306814,0.944291,0.119074;3.84415rad)
  shape: bbox 29.74 x 26.84 x 29.82 mm, 19 faces (baked)
FEATURE [Part::Feature] Clone001055  label="strutcap075"
  Placement = pos=(-866.791,606.199,1690.18) rot=(-0.037385,0.949845,-0.310478;3.97036rad)
  shape: bbox 31.57 x 26.83 x 26.72 mm, 19 faces (baked)
FEATURE [Part::Feature] Clone001056  label="strutcap076"
  Placement = pos=(-851.651,595.199,1701.75) rot=(-0.384951,0.662639,-0.642435;3.89838rad)
  shape: bbox 20.26 x 30.22 x 20.72 mm, 19 faces (baked)
FEATURE [Part::Feature] Cylinder028  label="Varilla-B-modif-010"
  Placement = pos=(-827.741,626.518,1701.75) rot=(0.456965,0.628961,0.628961;2.28433rad)
  shape: bbox 1134 x 376.9 x 10 mm, 3 faces (baked)
FEATURE [Part::Part2DObjectPython] Line061  # Draft 2D object (typed FeaturePython)
  ChamferSize = 0
  Closed = false
  End = (-850.675,-618.052,1701.28)
  FilletRadius = 0
  Length = 1236.1
  MakeFace = true
  Points = (2) [(-850.675,618.052,1701.28),(-850.675,-618.052,1701.28)]
  Start = (-850.675,618.052,1701.28)
  Subdivisions = 0
FEATURE [Part::Part2DObjectPython] Line062  # Draft 2D object (typed FeaturePython)
  ChamferSize = 0
  Closed = false
  End = (324.937,-1000.03,1701.28)
  FilletRadius = 0
  Length = 1236.11
  MakeFace = true
  Points = (2) [(-850.675,-618.052,1701.28),(324.937,-1000.03,1701.28)]
  Start = (-850.675,-618.052,1701.28)
  Subdivisions = 0
FEATURE [Part::Part2DObjectPython] Line063  # Draft 2D object (typed FeaturePython)
  ChamferSize = 0
  Closed = false
  End = (1051.49,1.332e-09,1701.28)
  FilletRadius = 0
  Length = 1236.1
  MakeFace = true
  Points = (2) [(324.929,1000.03,1701.28),(1051.49,1.3321e-09,1701.28)]
  Start = (324.929,1000.03,1701.28)
  Subdivisions = 0
FEATURE [Part::Part2DObjectPython] Line064  # Draft 2D object (typed FeaturePython)
  ChamferSize = 0
  Closed = false
  End = (324.937,-1000.03,1701.28)
  FilletRadius = 0
  Length = 1236.1
  MakeFace = true
  Points = (2) [(1051.49,1.3321e-09,1701.28),(324.937,-1000.03,1701.28)]
  Start = (1051.49,1.332e-09,1701.28)
  Subdivisions = 0
FEATURE [Part::Feature] Clone001057  label="strutcap077"
  Placement = pos=(-17.7984,-12.9315,1993.75) rot=(0.300929,-0.926151,0.227346;1.92056rad)
  shape: bbox 31.35 x 28.31 x 22.68 mm, 19 faces (baked)
FEATURE [Part::Feature] Cylinder029  label="Cylinder008"
  Placement = pos=(-17.7984,-12.9315,1993.75) rot=(0.376611,0.739148,-0.558413;3.69599rad)
  shape: bbox 821.2 x 600.3 x 295.8 mm, 3 faces (baked)
FEATURE [Part::Feature] Clone001058  label="Hub-019"
  Placement = pos=(-845.374,-614.211,1690.69) rot=(0.320391,0.016792,-0.947137;2.03872rad)
  shape: bbox 52.89 x 52.48 x 37.22 mm, 28 faces (baked)
FEATURE [Part::Feature] Clone001059  label="strutcap078"
  Placement = pos=(-851.64,-595.214,1701.75) rot=(0.399329,0.656651,0.639801;3.91882rad)
  shape: bbox 20.03 x 30.19 x 20.75 mm, 19 faces (baked)
FEATURE [Part::Feature] Clone001060  label="strutcap079"
  Placement = pos=(-866.78,-606.214,1690.18) rot=(0.055489,0.9504,0.306039;3.98098rad)
  shape: bbox 31.55 x 26.91 x 26.68 mm, 19 faces (baked)
FEATURE [Part::Feature] Clone001061  label="strutcap080"
  Placement = pos=(-832.872,-605.127,1707.53) rot=(0.591556,0.192211,0.783018;3.63986rad)
  shape: bbox 30.27 x 27.49 x 25.37 mm, 19 faces (baked)
FEATURE [Part::Feature] Clone001062  label="strutcap081"
  Placement = pos=(-829.243,-626.041,1701.75) rot=(0.652221,-0.288292,0.701067;3.2457rad)
  shape: bbox 31.36 x 25.86 x 20.72 mm, 19 faces (baked)
FEATURE [Part::Feature] Clone001063  label="strutcap082"
  Placement = pos=(-844.383,-637.041,1690.18) rot=(-0.545652,0.692057,-0.472568;3.4603rad)
  shape: bbox 22.9 x 32.27 x 26.72 mm, 19 faces (baked)
FEATURE [Part::Feature] Clone001064  label="strutcap083"
  Placement = pos=(-863.151,-627.127,1684.4) rot=(-0.306822,0.944288,-0.119077;3.84415rad)
  shape: bbox 29.74 x 26.84 x 29.82 mm, 19 faces (baked)
FEATURE [Part::Feature] Cylinder030  label="Varilla-B-modif-011"
  Placement = pos=(-851.641,-593.624,1701.75) rot=(-1e-06,0.707107,0.707107;3.1416rad)
  shape: bbox 10.01 x 1189 x 10 mm, 3 faces (baked)
FEATURE [Part::Feature] Clone001065  label="strutcap084"
  Placement = pos=(6.79873,-20.9232,1993.75) rot=(0.690296,-0.501521,0.521506;2.41724rad)
  shape: bbox 23.54 x 32.47 x 22.68 mm, 19 faces (baked)
FEATURE [App::DocumentObjectGroup] Group011  label="Clave"
  Group = -> [Clone001004,Clone,Clone001065,Clone001057,Clone001049,Clone001015]
FEATURE [Part::Feature] Cylinder031  label="Cylinder009"
  Placement = pos=(6.79873,-20.9232,1993.75) rot=(-0.125384,0.791599,-0.598038;2.95271rad)
  shape: bbox 320.8 x 962 x 295.8 mm, 3 faces (baked)
FEATURE [Part::Feature] Clone001066  label="Hub-020"
  Placement = pos=(322.923,-993.798,1690.69) rot=(0.482777,0.390952,-0.783634;0.910971rad)
  shape: bbox 55.11 x 51.63 x 37.22 mm, 28 faces (baked)
FEATURE [Part::Feature] Clone001067  label="strutcap085"
  Placement = pos=(318.147,-979.1,1707.53) rot=(-0.46391,-0.638529,-0.614059;1.7382rad)
  shape: bbox 23.11 x 31.33 x 25.37 mm, 19 faces (baked)
FEATURE [Part::Feature] Clone001068  label="strutcap086"
  Placement = pos=(302.919,-993.887,1701.75) rot=(0.077008,-0.937624,-0.339015;1.71438rad)
  shape: bbox 31.95 x 22.93 x 20.75 mm, 19 faces (baked)
FEATURE [Part::Feature] Clone001069  label="strutcap087"
  Placement = pos=(308.702,-1011.68,1690.18) rot=(-0.539571,0.841799,-0.015424;4.17481rad)
  shape: bbox 29.86 x 29.01 x 26.68 mm, 19 faces (baked)
FEATURE [Part::Feature] Clone001070  label="strutcap088"
  Placement = pos=(329.714,-1014.7,1684.4) rot=(0.771869,-0.560786,0.299561;2.713rad)
  shape: bbox 22.65 x 31.16 x 29.82 mm, 19 faces (baked)
FEATURE [Part::Feature] Clone001071  label="strutcap089"
  Placement = pos=(344.942,-999.909,1690.18) rot=(0.846307,-0.244693,0.47317;3.42288rad)
  shape: bbox 32.71 x 20 x 26.83 mm, 19 faces (baked)
FEATURE [Part::Feature] Clone001072  label="strutcap090"
  Placement = pos=(339.159,-982.111,1701.75) rot=(0.781158,0.168237,0.601239;4.08322rad)
  shape: bbox 29.92 x 30.42 x 20.72 mm, 19 faces (baked)
FEATURE [Part::Feature] Cylinder032  label="Varilla-B-modif-012"
  Placement = pos=(301.407,-993.395,1701.75) rot=(-0.456971,0.628958,0.628958;3.99886rad)
  shape: bbox 1134 x 376.9 x 10 mm, 3 faces (baked)
FEATURE [Part::Feature] Cylinder033  label="Varilla-B-modif-013"
  Placement = pos=(1037.92,-20.3126,1701.75) rot=(0.908667,-0.295233,-0.295233;1.66643rad)
  shape: bbox 706.8 x 967.7 x 10 mm, 3 faces (baked)
FEATURE [Part::Part2DObjectPython] Line065  # Draft 2D object (typed FeaturePython)
  ChamferSize = 0
  Closed = false
  End = (1376.39,-999.957,1051.5)
  FilletRadius = 0
  Length = 1236.03
  MakeFace = true
  Points = (2) [(324.937,-1000.03,1701.28),(1376.39,-999.957,1051.5)]
  Start = (324.937,-1000.03,1701.28)
  Subdivisions = 0
FEATURE [Part::Feature] Cylinder034  label="Varilla-B-modif-014"
  Placement = pos=(1357.36,-1000.76,1064.14) rot=(0.086928,-0.983946,-0.155865;1.03106rad)
  shape: bbox 1017 x 10.03 x 633.5 mm, 3 faces (baked)
FEATURE [Part::Feature] Clone001073  label="strutcap091"
  Placement = pos=(1357.54,-999.86,1064.43) rot=(0.250583,-0.868506,-0.427675;1.13881rad)
  shape: bbox 30.96 x 20.1 x 29.71 mm, 19 faces (baked)
FEATURE [Part::Feature] Cylinder035  label="Cylinder010"
  Placement = pos=(329.697,1014.7,1684.4) rot=(0.985873,-0.156147,0.060603;3.87249rad)
  shape: bbox 228.1 x 679.5 x 779.7 mm, 3 faces (baked)
FEATURE [Part::Feature] Cylinder036  label="Varilla-B-modif-015"
  Placement = pos=(1357.49,999.919,1064.43) rot=(-0.245397,-0.863791,0.440052;1.14636rad)
  shape: bbox 1017 x 10.05 x 633.5 mm, 3 faces (baked)
FEATURE [Part::Feature] Cylinder037  label="Varilla-B-modif-016"
  Placement = pos=(307.663,1011.8,1689.56) rot=(0.557122,0.830163,0.021082;4.15722rad)
  shape: bbox 824.6 x 603.3 x 634.3 mm, 3 faces (baked)
FEATURE [Part::Feature] Clone001074  label="strutcap092"
  Placement = pos=(344.925,999.915,1690.18) rot=(0.847741,0.241212,0.472389;2.87537rad)
  shape: bbox 32.7 x 20 x 26.9 mm, 19 faces (baked)
FEATURE [Part::Feature] Clone001075  label="strutcap093"
  Placement = pos=(329.697,1014.7,1684.4) rot=(0.771865,0.560793,0.299559;3.57019rad)
  shape: bbox 22.65 x 31.16 x 29.82 mm, 19 faces (baked)
FEATURE [Part::Feature] Clone001076  label="strutcap094"
  Placement = pos=(308.478,1011.53,1690.32) rot=(0.543251,0.839537,0.007414;4.18045rad)
  shape: bbox 29.9 x 28.94 x 26.61 mm, 19 faces (baked)
FEATURE [Part::Feature] Clone001077  label="strutcap095"
  Placement = pos=(1357.49,999.919,1064.43) rot=(-0.246268,-0.855952,0.454641;1.14624rad)
  shape: bbox 30.92 x 20 x 29.82 mm, 19 faces (baked)
FEATURE [Part::Feature] Cylinder038  label="Varilla-B-modif-017"
  Placement = pos=(-867.207,605.268,1689.56) rot=(-0.035573,0.954465,-0.296196;3.97386rad)
  shape: bbox 825.4 x 602.3 x 634.3 mm, 3 faces (baked)
FEATURE [Part::Feature] Cylinder039  label="Cylinder011"
  Placement = pos=(-863.157,627.12,1684.4) rot=(0.877489,0.447103,-0.173528;3.79809rad)
  shape: bbox 579.9 x 424.4 x 779.7 mm, 3 faces (baked)
FEATURE [Part::Feature] Cylinder040  label="Varilla-B-modif-018"
  Placement = pos=(-531.491,1600.04,1064.43) rot=(0.199138,-0.542979,0.815793;2.00203rad)
  shape: bbox 322.2 x 967.7 x 633.5 mm, 3 faces (baked)
FEATURE [Part::Feature] Cylinder041  label="Varilla-B-modif-019"
  Placement = pos=(-1685.97,-11.0365,1064.43) rot=(0.404604,-0.271467,0.87327;3.07625rad)
  shape: bbox 825.4 x 603.1 x 633.5 mm, 3 faces (baked)
FEATURE [Part::Feature] Cylinder042  label="Cylinder012"
  Placement = pos=(-863.157,-627.12,1684.4) rot=(0.42906,0.842077,-0.326825;3.47161rad)
  shape: bbox 579.9 x 424.4 x 779.7 mm, 3 faces (baked)
FEATURE [Part::Feature] Cylinder043  label="Varilla-B-modif-020"
  Placement = pos=(-843.626,-637.725,1689.56) rot=(-0.547223,0.697036,-0.463345;3.47876rad)
  shape: bbox 321.4 x 967.4 x 634.3 mm, 3 faces (baked)
FEATURE [Part::Feature] Cylinder044  label="Varilla-B-modif-021"
  Placement = pos=(-510.484,-1606.87,1064.43) rot=(0.55703,0.020822,0.830232;4.15797rad)
  shape: bbox 825.4 x 603 x 633.5 mm, 3 faces (baked)
FEATURE [Part::Feature] Cylinder045  label="Cylinder013"
  Placement = pos=(329.705,-1014.7,1684.4) rot=(-0.146074,0.922248,-0.35794;3.02833rad)
  shape: bbox 228.1 x 679.5 x 779.7 mm, 3 faces (baked)
FEATURE [Part::Feature] Cylinder046  label="Cylinder014"
  Placement = pos=(540.281,1707.78,876.414) rot=(0.752998,0.648404,-0.1121;3.71301rad)
  shape: bbox 538.6 x 295.9 x 862.3 mm, 3 faces (baked)
FEATURE [Part::Feature] Cylinder047  label="Cylinder015"
  Placement = pos=(565.816,1699.57,875.771) rot=(0.764557,0.607953,0.214116;2.70375rad)
  shape: bbox 604.8 x 89.65 x 862.6 mm, 3 faces (baked)
FEATURE [Part::Feature] Cylinder048  label="Varilla-B-modif-022"
  Placement = pos=(22.9176,1992.61,0) rot=(0.697446,0.506739,0.506739;1.92357rad)
  shape: bbox 1134 x 376.8 x 10 mm, 3 faces (baked)
FEATURE [Part::Feature] Cylinder049  label="Cylinder016"
  Placement = pos=(-1457.24,1041.57,876.414) rot=(0.221853,0.940826,-0.256178;3.47269rad)
  shape: bbox 445.1 x 424.7 x 862.3 mm, 3 faces (baked)
FEATURE [Part::Feature] Cylinder050  label="Varilla-B-modif-023"
  Placement = pos=(-1888,637.545,0) rot=(0.223909,0.689153,0.689153;2.70104rad)
  shape: bbox 706.8 x 967.7 x 10 mm, 3 faces (baked)
FEATURE [Part::Feature] Cylinder051  label="Cylinder017"
  Placement = pos=(-1441.54,1063.32,875.771) rot=(0.255317,0.92006,0.297158;3.03584rad)
  shape: bbox 269.8 x 551.3 x 862.6 mm, 3 faces (baked)
FEATURE [Part::Feature] Cylinder052  label="Varilla-B-modif-024"
  Placement = pos=(-1189.77,-1598.58,0) rot=(-0.223929,0.68915,0.68915;3.58218rad)
  shape: bbox 706.9 x 967.6 x 10 mm, 3 faces (baked)
FEATURE [Part::Feature] Cylinder053  label="Cylinder018"
  Placement = pos=(-1440.9,-1064.05,876.414) rot=(-0.368456,0.879459,-0.301316;3.11119rad)
  shape: bbox 270.1 x 551.7 x 862.3 mm, 3 faces (baked)
FEATURE [Part::Feature] Cylinder054  label="Cylinder019"
  Placement = pos=(-1456.73,-1042.4,875.771) rot=(-0.336706,0.901009,0.273516;3.40569rad)
  shape: bbox 444.9 x 424.3 x 862.6 mm, 3 faces (baked)
FEATURE [Part::Feature] Cylinder055  label="Cylinder020"
  Placement = pos=(541.239,-1707.55,875.771) rot=(0.824708,-0.546051,-0.147262;2.60334rad)
  shape: bbox 538.1 x 295.8 x 862.6 mm, 3 faces (baked)
FEATURE [Part::Feature] Cylinder056  label="Varilla-B-modif-025"
  Placement = pos=(1152.7,-1625.51,0) rot=(0.69747,-0.506723,-0.506723;1.92354rad)
  shape: bbox 1134 x 376.9 x 10 mm, 3 faces (baked)
FEATURE [Part::Feature] Cylinder057  label="Cylinder021"
  Placement = pos=(566.724,-1699.19,876.414) rot=(0.829948,-0.503984,0.239135;3.52267rad)
  shape: bbox 605.2 x 89.84 x 862.3 mm, 3 faces (baked)
FEATURE [Part::Feature] Clone001078  label="strutcap096"
  Placement = pos=(530.378,1699.18,898.82) rot=(-0.414259,-0.732085,0.540778;1.78299rad)
  shape: bbox 30.96 x 20.14 x 22.38 mm, 19 faces (baked)
FEATURE [Part::Feature] Clone001079  label="strutcap097"
  Placement = pos=(540.273,1707.74,876.408) rot=(0.753174,0.648286,-0.111595;3.71391rad)
  shape: bbox 26.59 x 25.55 x 30.67 mm, 19 faces (baked)
FEATURE [Part::Feature] Clone001080  label="strutcap098"
  Placement = pos=(565.808,1699.53,875.769) rot=(0.764338,0.608049,0.214624;2.70459rad)
  shape: bbox 28.6 x 20 x 30.68 mm, 19 faces (baked)
FEATURE [Part::Feature] Clone001081  label="strutcap099"
  Placement = pos=(570.601,1687.09,896.949) rot=(0.782815,0.102142,0.613814;1.95118rad)
  shape: bbox 32 x 28.57 x 22.88 mm, 19 faces (baked)
FEATURE [Part::Feature] Clone001082  label="strutcap100"
  Placement = pos=(548.01,1686.6,911.365) rot=(0.323892,-0.445799,0.83448;1.43273rad)
  shape: bbox 21.5 x 28.59 x 31.71 mm, 19 faces (baked)
FEATURE [Part::Feature] Clone001083  label="Hub5-01-clave004"
  Placement = pos=(549.337,1690.68,888.915) rot=(0.403006,0.403003,0.82169;3.9346rad)
  shape: bbox 54.11 x 37.29 x 51.33 mm, 25 faces (baked)
FEATURE [Part::Feature] Clone001084  label="Hub5-01-clave005"
  Placement = pos=(-1438.18,1044.9,888.915) rot=(-0.126077,-0.795998,-0.592023;1.42128rad)
  shape: bbox 45.2 x 49.91 x 51.33 mm, 25 faces (baked)
FEATURE [Part::Feature] Clone001085  label="strutcap101"
  Placement = pos=(-1457.21,1041.55,876.408) rot=(0.222054,0.940813,-0.256052;3.47399rad)
  shape: bbox 28.2 x 24.81 x 30.67 mm, 19 faces (baked)
FEATURE [Part::Feature] Clone001086  label="strutcap102"
  Placement = pos=(-1441.51,1063.3,875.769) rot=(0.255103,0.920065,0.297325;3.03711rad)
  shape: bbox 22.21 x 29.03 x 30.68 mm, 19 faces (baked)
FEATURE [Part::Feature] Clone001087  label="strutcap103"
  Placement = pos=(-1428.19,1064.01,896.949) rot=(0.480485,0.454913,0.749792;2.83064rad)
  shape: bbox 30.89 x 29.5 x 22.88 mm, 19 faces (baked)
FEATURE [Part::Feature] Clone001088  label="strutcap104"
  Placement = pos=(-1434.71,1042.38,911.365) rot=(0.359362,-0.116764,0.925865;2.55715rad)
  shape: bbox 27.2 x 24.82 x 31.71 mm, 19 faces (baked)
FEATURE [Part::Feature] Clone001089  label="strutcap105"
  Placement = pos=(-1452.12,1029.49,898.82) rot=(0.076698,-0.673574,0.735129;2.61355rad)
  shape: bbox 25.23 x 31.29 x 22.38 mm, 19 faces (baked)
FEATURE [Part::Feature] Clone001090  label="Hub5-01-clave006"
  Placement = pos=(-1438.18,-1044.9,888.915) rot=(0.440106,-0.863765,0.245392;1.14634rad)
  shape: bbox 45.2 x 49.91 x 51.33 mm, 25 faces (baked)
FEATURE [Part::Feature] Clone001091  label="strutcap106"
  Placement = pos=(-1456.71,-1042.38,875.769) rot=(-0.336923,0.900992,0.273307;3.40693rad)
  shape: bbox 28.13 x 24.8 x 30.68 mm, 19 faces (baked)
FEATURE [Part::Feature] Clone001092  label="strutcap107"
  Placement = pos=(-1453.27,-1029.49,896.949) rot=(0.126083,0.675935,0.726096;3.77224rad)
  shape: bbox 25.11 x 31.29 x 22.88 mm, 19 faces (baked)
FEATURE [Part::Feature] Clone001093  label="strutcap108"
  Placement = pos=(-1434.71,-1042.38,911.365) rot=(0.359362,0.116764,0.925865;3.72603rad)
  shape: bbox 27.2 x 24.82 x 31.71 mm, 19 faces (baked)
FEATURE [Part::Feature] Clone001094  label="strutcap109"
  Placement = pos=(-1427.84,-1062.91,898.82) rot=(0.451787,-0.493106,0.743461;3.55656rad)
  shape: bbox 30.89 x 29.64 x 22.38 mm, 19 faces (baked)
FEATURE [Part::Feature] Clone001095  label="strutcap110"
  Placement = pos=(-1440.88,-1064.03,876.408) rot=(-0.368245,0.879462,-0.301567;3.11241rad)
  shape: bbox 22.22 x 29.51 x 30.67 mm, 19 faces (baked)
FEATURE [Part::Feature] Clone001096  label="Hub5-01-clave007"
  Placement = pos=(549.351,-1690.68,888.915) rot=(0.58635,-0.29876,0.752952;1.85083rad)
  shape: bbox 54.11 x 37.29 x 51.33 mm, 25 faces (baked)
FEATURE [Part::Feature] Clone001097  label="strutcap111"
  Placement = pos=(530.035,-1700.27,896.949) rot=(0.372241,-0.78273,-0.49877;1.70887rad)
  shape: bbox 30.96 x 20.06 x 22.88 mm, 19 faces (baked)
FEATURE [Part::Feature] Clone001098  label="strutcap112"
  Placement = pos=(541.226,-1707.52,875.769) rot=(0.824895,-0.545917,-0.146708;2.60259rad)
  shape: bbox 26.57 x 25.89 x 30.68 mm, 19 faces (baked)
FEATURE [Part::Feature] Clone001099  label="strutcap113"
  Placement = pos=(548.024,-1686.6,911.365) rot=(-0.323892,-0.445802,-0.834479;1.43272rad)
  shape: bbox 21.5 x 28.59 x 31.71 mm, 19 faces (baked)
FEATURE [Part::Feature] Clone001100  label="strutcap114"
  Placement = pos=(569.68,-1686.41,898.82) rot=(-0.797368,0.162279,-0.581265;1.86885rad)
  shape: bbox 32.15 x 28.57 x 22.38 mm, 19 faces (baked)
FEATURE [Part::Feature] Clone001101  label="strutcap115"
  Placement = pos=(566.711,-1699.15,876.408) rot=(0.829728,-0.504084,0.239691;3.52197rad)
  shape: bbox 29.43 x 20.13 x 30.67 mm, 19 faces (baked)
FEATURE [Part::Feature] Clone001102  label="Hub-021"
  Placement = pos=(-522.419,1607.96,1044.94) rot=(-0.404151,-0.556253,-0.726117;1.57141rad)
  shape: bbox 54.14 x 40.13 x 50.11 mm, 28 faces (baked)
FEATURE [Part::Feature] Clone001105  label="strutcap118"
  Placement = pos=(-516.067,1625.93,1032.31) rot=(0.655766,0.705688,0.268283;3.03581rad)
  shape: bbox 25.3 x 25.97 x 30.96 mm, 19 faces (baked)
FEATURE [Part::Feature] Clone001106  label="strutcap119"
  Placement = pos=(-503.124,1619.77,1048.2) rot=(0.67398,0.417938,0.609162;2.53046rad)
  shape: bbox 30.99 x 22.33 x 20.3 mm, 19 faces (baked)
FEATURE [Part::Feature] Clone001107  label="strutcap120"
  Placement = pos=(-510.484,1606.82,1064.4) rot=(0.551632,-0.035834,0.833318;2.11859rad)
  shape: bbox 28.95 x 26.75 x 29.86 mm, 19 faces (baked)
FEATURE [Part::Feature] Clone001108  label="strutcap121"
  Placement = pos=(-531.49,1600.04,1064.43) rot=(0.195018,-0.537301,0.820534;2.01296rad)
  shape: bbox 24.18 x 30.56 x 29.82 mm, 19 faces (baked)
FEATURE [Part::Feature] Clone001109  label="Hub-022"
  Placement = pos=(-1690.7,0.0372864,1044.94) rot=(-1.1e-05,-1,-2e-05;1.01578rad)
  shape: bbox 37.43 x 53.16 x 50.11 mm, 28 faces (baked)
FEATURE [Part::Feature] Clone001111  label="strutcap123"
  Placement = pos=(-1705.82,11.6304,1032.31) rot=(0.116339,0.961371,0.249462;3.3715rad)
  shape: bbox 23.88 x 27.32 x 30.96 mm, 19 faces (baked)
FEATURE [Part::Feature] Clone001112  label="strutcap124"
  Placement = pos=(-1695.97,22.0374,1048.2) rot=(0.287109,0.703654,0.649954;3.33809rad)
  shape: bbox 21.94 x 32.05 x 20.3 mm, 19 faces (baked)
FEATURE [Part::Feature] Clone001113  label="strutcap125"
  Placement = pos=(-1685.93,11.0372,1064.4) rot=(0.407724,0.257586,0.87602;3.20384rad)
  shape: bbox 29.33 x 26.91 x 29.86 mm, 19 faces (baked)
FEATURE [Part::Feature] Clone001114  label="strutcap126"
  Placement = pos=(-1685.97,-11.0364,1064.43) rot=(0.40029,-0.270519,0.87555;3.09124rad)
  shape: bbox 29.19 x 27.26 x 29.82 mm, 19 faces (baked)
FEATURE [Part::Feature] Clone001116  label="Hub-023"
  Placement = pos=(-522.49,-1607.94,1044.94) rot=(0.404145,-0.55627,0.726106;1.57137rad)
  shape: bbox 54.14 x 40.13 x 50.11 mm, 28 faces (baked)
FEATURE [Part::Feature] Clone001117  label="strutcap128"
  Placement = pos=(-510.498,-1606.87,1064.43) rot=(0.555204,0.018892,0.8315;4.17521rad)
  shape: bbox 29.12 x 26.51 x 29.82 mm, 19 faces (baked)
FEATURE [Part::Feature] Clone001118  label="strutcap129"
  Placement = pos=(-531.478,-1600,1064.4) rot=(-0.211892,-0.532008,-0.819798;2.00111rad)
  shape: bbox 23.74 x 30.6 x 29.86 mm, 19 faces (baked)
FEATURE [Part::Feature] Clone001119  label="strutcap130"
  Placement = pos=(-545.042,-1606.15,1048.2) rot=(-0.203171,0.82696,0.52427;4.09656rad)
  shape: bbox 32.67 x 26.78 x 20.3 mm, 19 faces (baked)
FEATURE [Part::Feature] Clone001120  label="strutcap131"
  Placement = pos=(-538.189,-1618.74,1032.31) rot=(-0.481748,0.865531,0.13702;3.62315rad)
  shape: bbox 28.95 x 20.82 x 30.96 mm, 19 faces (baked)
FEATURE [Part::Feature] Cylinder058  label="Cylinder022"
  Placement = pos=(530.378,1699.21,898.834) rot=(-0.413717,-0.732343,0.540844;1.78399rad)
  shape: bbox 1035 x 89.07 x 159.4 mm, 3 faces (baked)
FEATURE [Part::Feature] Cylinder059  label="Cylinder023"
  Placement = pos=(570.617,1687.11,896.969) rot=(0.783276,0.101681,0.613303;1.95105rad)
  shape: bbox 795.2 x 679.7 x 161.3 mm, 3 faces (baked)
FEATURE [Part::Feature] Cylinder060  label="Varilla-B-modif-026"
  Placement = pos=(1372.43,1012.12,1030.9) rot=(0.616123,0.772286,0.154811;3.60091rad)
  shape: bbox 201.9 x 602.9 x 1017 mm, 3 faces (baked)
FEATURE [Part::Feature] Clone001123  label="strutcap134"
  Placement = pos=(1359.16,1014.63,1048.2) rot=(-0.756432,-0.638991,0.139644;1.73831rad)
  shape: bbox 30 x 31.16 x 20.3 mm, 19 faces (baked)
FEATURE [Part::Feature] Clone001124  label="strutcap135"
  Placement = pos=(1373.75,1011.64,1032.01) rot=(0.909322,0.414351,0.038035;3.6661rad)
  shape: bbox 20.28 x 29.06 x 31.05 mm, 19 faces (baked)
FEATURE [Part::Feature] Clone001125  label="Hub-024"
  Placement = pos=(1167.88,1607.21,0) rot=(-0.413351,0.811346,0.413351;1.77835rad)
  shape: bbox 48.34 x 39.86 x 55.6 mm, 28 faces (baked)
FEATURE [Part::Feature] Clone001126  label="strutcap136"
  Placement = pos=(1162.63,1618.69,19.0526) rot=(-0.354648,-0.474559,0.805617;1.14619rad)
  shape: bbox 28.01 x 22.72 x 31.69 mm, 19 faces (baked)
FEATURE [Part::Feature] Clone001127  label="strutcap137"
  Placement = pos=(1153.73,1625.15,0) rot=(-0.697483,-0.506713,0.506713;1.92352rad)
  shape: bbox 31.34 x 25.98 x 20 mm, 19 faces (baked)
FEATURE [Part::Feature] Clone001128  label="strutcap138"
  Placement = pos=(1180.54,1607.1,19.8831) rot=(0.632762,0.03188,0.77369;0.99253rad)
  shape: bbox 25.27 x 26.79 x 31.62 mm, 19 faces (baked)
FEATURE [Part::Feature] Clone001129  label="strutcap139"
  Placement = pos=(1189.16,1599.52,0) rot=(0.908302,0.295794,0.295794;1.66683rad)
  shape: bbox 30.1 x 30.58 x 20 mm, 19 faces (baked)
FEATURE [Part::Feature] Cylinder061  label="Varilla-B-modif-027"
  Placement = pos=(1189.84,1598.52,0) rot=(0.908667,0.295233,0.295233;1.66643rad)
  shape: bbox 706.8 x 967.7 x 10 mm, 3 faces (baked)
FEATURE [Part::Feature] Cylinder062  label="Varilla-B-modif-028"
  Placement = pos=(-538.473,1618.02,1030.9) rot=(0.045055,0.998909,-0.012317;3.69415rad)
  shape: bbox 633 x 11.04 x 1017 mm, 3 faces (baked)
FEATURE [Part::Feature] Cylinder063  label="Varilla-B-modif-029"
  Placement = pos=(-10.1769,1992.61,20.4541) rot=(0.167218,-0.60597,0.777714;0.899398rad)
  shape: bbox 514.7 x 376.9 x 1017 mm, 3 faces (baked)
FEATURE [Part::Feature] Cylinder064  label="Cylinder024"
  Placement = pos=(-1428.21,1064.04,896.969) rot=(0.481026,0.454827,0.749497;2.83001rad)
  shape: bbox 888.2 x 550.9 x 161.3 mm, 3 faces (baked)
FEATURE [Part::Feature] Clone001130  label="strutcap140"
  Placement = pos=(-544.971,1606.18,1048.2) rot=(0.203272,0.826904,-0.52432;4.09647rad)
  shape: bbox 32.67 x 26.78 x 20.3 mm, 19 faces (baked)
FEATURE [Part::Feature] Clone001131  label="strutcap141"
  Placement = pos=(-537.612,1619.12,1032.01) rot=(0.488533,0.863387,-0.126091;3.6085rad)
  shape: bbox 28.61 x 21.1 x 31.05 mm, 19 faces (baked)
FEATURE [Part::Feature] Cylinder065  label="Cylinder025"
  Placement = pos=(-1453.3,-1029.5,896.969) rot=(0.126564,0.676057,0.725898;3.77131rad)
  shape: bbox 252.7 x 1010 x 161.3 mm, 3 faces (baked)
FEATURE [Part::Feature] Cylinder066  label="Cylinder026"
  Placement = pos=(-1452.15,1029.5,898.834) rot=(0.077196,-0.673675,0.734984;2.61448rad)
  shape: bbox 253.8 x 1010 x 159.4 mm, 3 faces (baked)
FEATURE [Part::Feature] Cylinder067  label="Varilla-B-modif-030"
  Placement = pos=(-1898.23,606.07,20.4541) rot=(0.251906,-0.2009,0.946669;2.02469rad)
  shape: bbox 203 x 603 x 1017 mm, 3 faces (baked)
FEATURE [Part::Feature] Cylinder068  label="Varilla-B-modif-031"
  Placement = pos=(-1705.23,-12.1218,1030.9) rot=(-0.54234,0.821957,-0.173938;3.57234rad)
  shape: bbox 203.8 x 602.3 x 1017 mm, 3 faces (baked)
FEATURE [Part::Feature] Clone001132  label="strutcap142"
  Placement = pos=(-1695.97,-21.9626,1048.2) rot=(-0.287012,0.703678,-0.64997;3.33796rad)
  shape: bbox 21.94 x 32.05 x 20.3 mm, 19 faces (baked)
FEATURE [Part::Feature] Clone001133  label="strutcap143"
  Placement = pos=(-1706.01,-10.9624,1032.01) rot=(-0.109939,0.96532,-0.236791;3.37221rad)
  shape: bbox 24.01 x 26.91 x 31.05 mm, 19 faces (baked)
FEATURE [Part::Feature] Cylinder069  label="Cylinder027"
  Placement = pos=(-1427.84,-1062.95,898.834) rot=(0.452335,-0.492994,0.743203;3.55725rad)
  shape: bbox 887.9 x 551.9 x 159.4 mm, 3 faces (baked)
FEATURE [Part::Feature] Cylinder070  label="Cylinder028"
  Placement = pos=(530.036,-1700.3,896.969) rot=(0.371723,-0.782962,-0.498791;1.70995rad)
  shape: bbox 1035 x 90.15 x 161.3 mm, 3 faces (baked)
FEATURE [Part::Feature] Cylinder071  label="Varilla-B-modif-032"
  Placement = pos=(-515.403,-1625.52,1030.9) rot=(0.903009,-0.3391,0.263791;2.99542rad)
  shape: bbox 513.7 x 377.4 x 1017 mm, 3 faces (baked)
FEATURE [Part::Feature] Cylinder072  label="Varilla-B-modif-033"
  Placement = pos=(-1162.98,-1618.04,20.4541) rot=(0.273237,-0.012278,0.961868;3.22808rad)
  shape: bbox 633.5 x 10.03 x 1017 mm, 3 faces (baked)
FEATURE [Part::Feature] Clone001134  label="strutcap144"
  Placement = pos=(-503.182,-1619.75,1048.2) rot=(0.673934,-0.418028,0.609152;3.75287rad)
  shape: bbox 30.99 x 22.33 x 20.3 mm, 19 faces (baked)
FEATURE [Part::Feature] Clone001135  label="strutcap145"
  Placement = pos=(-516.746,-1625.9,1032.01) rot=(-0.652655,0.712308,-0.258186;3.0512rad)
  shape: bbox 24.88 x 26 x 31.05 mm, 19 faces (baked)
FEATURE [Part::Feature] Cylinder073  label="Cylinder029"
  Placement = pos=(569.712,-1686.43,898.834) rot=(-0.797837,0.161779,-0.580762;1.86862rad)
  shape: bbox 796.1 x 679.1 x 159.4 mm, 3 faces (baked)
FEATURE [Part::Feature] Cylinder074  label="Varilla-B-modif-034"
  Placement = pos=(1179.48,-1606.05,20.4541) rot=(-0.285022,-0.188133,-0.939877;1.85504rad)
  shape: bbox 203 x 603.1 x 1017 mm, 3 faces (baked)
FEATURE [Part::Feature] Clone001136  label="Hub-025"
  Placement = pos=(0.0486416,1986.72,0) rot=(-0.577341,0.577369,0.577341;2.09437rad)
  shape: bbox 53.16 x 12.4 x 55.6 mm, 28 faces (baked)
FEATURE [Part::Feature] Clone001137  label="strutcap146"
  Placement = pos=(-21.9511,1992.92,0) rot=(0.456975,0.628957,-0.628957;3.99887rad)
  shape: bbox 32.2 x 23.31 x 20 mm, 19 faces (baked)
FEATURE [Part::Feature] Clone001138  label="strutcap147"
  Placement = pos=(-10.9511,1992.92,19.0526) rot=(-0.043067,-0.321506,0.945927;1.61128rad)
  shape: bbox 24.46 x 22.68 x 32.46 mm, 19 faces (baked)
FEATURE [Part::Feature] Clone001139  label="strutcap148"
  Placement = pos=(10.3528,1994.07,19.8831) rot=(0.407648,0.155548,0.899793;1.52684rad)
  shape: bbox 27.6 x 22.68 x 31.62 mm, 19 faces (baked)
FEATURE [Part::Feature] Clone001140  label="strutcap149"
  Placement = pos=(21.7815,1993.01,0) rot=(0.696937,0.507089,0.507089;1.92426rad)
  shape: bbox 32.2 x 23.29 x 20 mm, 19 faces (baked)
FEATURE [Part::Feature] Cylinder075  label="Varilla-B-modif-035"
  Placement = pos=(-1152.6,1625.58,0) rot=(0.456975,0.628957,0.628957;2.28431rad)
  shape: bbox 1134 x 376.9 x 10 mm, 3 faces (baked)
FEATURE [Part::Feature] Clone001141  label="Hub-026"
  Placement = pos=(-1889.47,613.977,0) rot=(-0.702712,0.111316,0.702712;2.91987rad)
  shape: bbox 27.47 x 52.09 x 55.6 mm, 28 faces (baked)
FEATURE [Part::Feature] Clone001142  label="strutcap150"
  Placement = pos=(-1898.77,605.432,19.0526) rot=(0.112612,-0.208529,0.971511;2.82156rad)
  shape: bbox 20.37 x 25.38 x 32.46 mm, 19 faces (baked)
FEATURE [Part::Feature] Clone001143  label="strutcap151"
  Placement = pos=(-1902.17,594.971,0) rot=(8e-06,0.707107,-0.707107;3.14161rad)
  shape: bbox 20.3 x 30 x 20 mm, 19 faces (baked)
FEATURE [Part::Feature] Clone001144  label="strutcap152"
  Placement = pos=(-1893.28,626.049,19.8831) rot=(0.168898,0.258947,0.95101;2.70038rad)
  shape: bbox 25.15 x 27.06 x 31.62 mm, 19 faces (baked)
FEATURE [Part::Feature] Clone001145  label="strutcap153"
  Placement = pos=(-1888.73,636.589,0) rot=(0.22342,0.689233,0.689233;2.70197rad)
  shape: bbox 27.81 x 32.24 x 20 mm, 19 faces (baked)
FEATURE [Part::Feature] Clone001146  label="Hub-027"
  Placement = pos=(-1167.76,1607.29,0) rot=(-0.665244,0.33897,0.665244;2.48796rad)
  shape: bbox 48.34 x 39.85 x 55.6 mm, 28 faces (baked)
FEATURE [Part::Feature] Clone001147  label="strutcap154"
  Placement = pos=(-1180.31,1605.85,19.0526) rot=(0.047109,-0.257408,0.965154;2.21275rad)
  shape: bbox 22.76 x 25.45 x 32.46 mm, 19 faces (baked)
FEATURE [Part::Feature] Clone001148  label="strutcap155"
  Placement = pos=(-1189.21,1599.38,0) rot=(0.223919,0.689152,-0.689152;3.58216rad)
  shape: bbox 30.09 x 30.59 x 20 mm, 19 faces (baked)
FEATURE [Part::Feature] Clone001149  label="strutcap156"
  Placement = pos=(-1163.75,1619.3,19.8831) rot=(0.270223,0.217936,0.937808;2.10624rad)
  shape: bbox 27.56 x 22.35 x 31.62 mm, 19 faces (baked)
FEATURE [Part::Feature] Clone001150  label="strutcap157"
  Placement = pos=(-1153.87,1625.15,0) rot=(0.456433,0.629154,0.629154;2.28521rad)
  shape: bbox 31.34 x 26 x 20 mm, 19 faces (baked)
FEATURE [Part::Feature] Cylinder076  label="Varilla-B-modif-036"
  Placement = pos=(-1902.18,-593.911,0) rot=(-2e-06,0.707107,0.707107;3.1416rad)
  shape: bbox 10.01 x 1189 x 10 mm, 3 faces (baked)
FEATURE [Part::Feature] Clone001151  label="Hub-028"
  Placement = pos=(-1889.51,-613.843,0) rot=(-0.702716,-0.111274,0.702716;3.36323rad)
  shape: bbox 27.47 x 52.09 x 55.6 mm, 28 faces (baked)
FEATURE [Part::Feature] Clone001152  label="strutcap158"
  Placement = pos=(-1888.61,-636.682,0) rot=(-0.223903,0.689154,-0.689154;2.70105rad)
  shape: bbox 27.82 x 32.23 x 20 mm, 19 faces (baked)
FEATURE [Part::Feature] Clone001153  label="strutcap159"
  Placement = pos=(-1892.01,-626.22,19.0526) rot=(0.171151,-0.163157,0.971641;3.43228rad)
  shape: bbox 24.41 x 24.08 x 32.46 mm, 19 faces (baked)
FEATURE [Part::Feature] Clone001154  label="strutcap160"
  Placement = pos=(-1899.69,-606.315,19.8831) rot=(0.078906,0.292136,0.953116;3.29902rad)
  shape: bbox 20 x 27.5 x 31.62 mm, 19 faces (baked)
FEATURE [Part::Feature] Clone001155  label="strutcap161"
  Placement = pos=(-1902.21,-595.116,0) rot=(-0.00048,0.707107,0.707107;3.14255rad)
  shape: bbox 20.33 x 30.01 x 20 mm, 19 faces (baked)
FEATURE [Part::Feature] Clone001156  label="Hub-029"
  Placement = pos=(-1167.81,-1607.26,0) rot=(-0.665251,-0.338942,0.665251;3.79517rad)
  shape: bbox 48.34 x 39.86 x 55.6 mm, 28 faces (baked)
FEATURE [Part::Feature] Clone001157  label="strutcap162"
  Placement = pos=(-1180.46,-1607.15,19.8831) rot=(-0.016336,0.32408,0.945889;3.89619rad)
  shape: bbox 25.27 x 26.79 x 31.62 mm, 19 faces (baked)
FEATURE [Part::Feature] Clone001158  label="strutcap163"
  Placement = pos=(-1189.08,-1599.57,0) rot=(-0.224418,0.689071,0.689071;3.58311rad)
  shape: bbox 30.1 x 30.58 x 20 mm, 19 faces (baked)
FEATURE [Part::Feature] Clone001159  label="strutcap164"
  Placement = pos=(-1162.55,-1618.75,19.0526) rot=(0.234252,-0.112384,0.965658;4.04131rad)
  shape: bbox 25.78 x 20.67 x 32.46 mm, 19 faces (baked)
FEATURE [Part::Feature] Clone001160  label="strutcap165"
  Placement = pos=(-1153.65,-1625.21,0) rot=(-0.456958,0.628963,-0.628963;2.28434rad)
  shape: bbox 31.34 x 25.98 x 20 mm, 19 faces (baked)
FEATURE [Part::Feature] Cylinder077  label="Varilla-B-modif-037"
  Placement = pos=(-22.8736,-1992.61,0) rot=(-0.456985,0.628953,0.628953;3.99889rad)
  shape: bbox 1134 x 376.8 x 10 mm, 3 faces (baked)
FEATURE [Part::Feature] Clone001161  label="Hub-030"
  Placement = pos=(0.0119054,-1986.72,0) rot=(-0.577354,-0.577343,0.577354;4.18878rad)
  shape: bbox 53.16 x 12.4 x 55.6 mm, 28 faces (baked)
FEATURE [Part::Feature] Clone001162  label="strutcap166"
  Placement = pos=(-10.292,-1994.07,19.8831) rot=(0.137371,-0.359993,-0.922786;1.79868rad)
  shape: bbox 27.6 x 22.68 x 31.62 mm, 19 faces (baked)
FEATURE [Part::Feature] Clone001163  label="strutcap167"
  Placement = pos=(11.0118,-1992.92,19.0526) rot=(-0.317192,0.042484,-0.947409;1.63983rad)
  shape: bbox 24.46 x 22.68 x 32.46 mm, 19 faces (baked)
FEATURE [Part::Feature] Clone001164  label="strutcap168"
  Placement = pos=(22.0118,-1992.92,0) rot=(-0.69746,0.50673,-0.50673;1.92355rad)
  shape: bbox 32.2 x 23.31 x 20 mm, 19 faces (baked)
FEATURE [Part::Feature] Clone001165  label="strutcap169"
  Placement = pos=(-21.7208,-1993.01,0) rot=(-0.457503,0.628765,0.628765;3.99974rad)
  shape: bbox 32.2 x 23.29 x 20 mm, 19 faces (baked)
FEATURE [Part::Feature] Clone001166  label="Hub-031"
  Placement = pos=(1167.8,-1607.27,0) rot=(0.413386,0.81131,-0.413386;1.77839rad)
  shape: bbox 48.34 x 39.86 x 55.6 mm, 28 faces (baked)
FEATURE [Part::Feature] Clone001167  label="strutcap170"
  Placement = pos=(1163.78,-1619.27,19.8831) rot=(0.326774,-0.405165,-0.85385;1.23636rad)
  shape: bbox 27.56 x 22.35 x 31.62 mm, 19 faces (baked)
FEATURE [Part::Feature] Clone001168  label="strutcap171"
  Placement = pos=(1180.34,-1605.82,19.0526) rot=(-0.455439,-0.083356,-0.886356;1.05951rad)
  shape: bbox 22.76 x 25.45 x 32.46 mm, 19 faces (baked)
FEATURE [Part::Feature] Clone001169  label="strutcap172"
  Placement = pos=(1153.91,-1625.13,0) rot=(0.697993,-0.506363,-0.506363;1.92284rad)
  shape: bbox 31.34 x 26 x 20 mm, 19 faces (baked)
FEATURE [Part::Feature] Clone001170  label="strutcap173"
  Placement = pos=(1189.24,-1599.35,0) rot=(-0.908667,0.295233,-0.295233;1.66643rad)
  shape: bbox 30.09 x 30.59 x 20 mm, 19 faces (baked)
FEATURE [Part::Feature] Cylinder078  label="Varilla-B-modif-038"
  Placement = pos=(1888.01,-637.504,0) rot=(0.908674,-0.295221,-0.295221;1.66642rad)
  shape: bbox 706.8 x 967.7 x 10 mm, 3 faces (baked)
FEATURE [App::DocumentObjectGroup] Group010  label="Estructura"
  Group = -> [Clone031,Clone030,Clone028,Cylinder014,Group011,Clone001005,Clone001006,Clone001010,Cylinder016,Clone002,Clone007,Clone005,Clone008,Clone009,Clone001012,Clone001013,Cylinder017,Clone001007,Clone001014,Clone001009,Clone001008,Cylinder015,Cylinder018,Cylinder020,Cylinder019,Clone001016,Clone001020,Clone001018,Clone001023,Clone001027,Cylinder021,Cylinder022,Clone001031,Clone001030,Clone001033,+181 more]
FEATURE [Part::Part2DObjectPython] Line066  # Draft 2D object (typed FeaturePython)
  ChamferSize = 0
  Closed = false
  End = (324.929,1000.03,1701.28)
  FilletRadius = 0
  Length = 1236.04
  MakeFace = true
  Points = (2) [(1376.39,999.957,1051.5),(324.929,1000.03,1701.28)]
  Start = (1376.39,999.957,1051.5)
  Subdivisions = 0
FEATURE [Part::Part2DObjectPython] Line067  # Draft 2D object (typed FeaturePython)
  ChamferSize = 0
  Closed = false
  End = (1376.39,999.957,1051.5)
  FilletRadius = 0
  Length = 1236.04
  MakeFace = true
  Points = (2) [(324.929,1000.03,1701.28),(1376.39,999.957,1051.5)]
  Start = (324.929,1000.03,1701.28)
  Subdivisions = 0
FEATURE [Part::Part2DObjectPython] Line068  # Draft 2D object (typed FeaturePython)
  ChamferSize = 0
  Closed = false
  End = (552.796,1701.28,894.456)
  FilletRadius = 0
  Length = 1093.08
  MakeFace = true
  Points = (2) [(1376.39,999.957,1051.5),(552.796,1701.28,894.456)]
  Start = (1376.39,999.957,1051.5)
  Subdivisions = 0
FEATURE [Part::Part2DObjectPython] Line069  # Draft 2D object (typed FeaturePython)
  ChamferSize = 0
  Closed = false
  End = (552.796,1701.28,894.456)
  FilletRadius = 0
  Length = 1093
  MakeFace = true
  Points = (2) [(324.929,1000.03,1701.28),(552.796,1701.28,894.456)]
  Start = (324.929,1000.03,1701.28)
  Subdivisions = 0
FEATURE [Part::Part2DObjectPython] Line070  # Draft 2D object (typed FeaturePython)
  ChamferSize = 0
  Closed = false
  End = (-525.738,1618.01,1051.5)
  FilletRadius = 0
  Length = 1093.08
  MakeFace = true
  Points = (2) [(552.796,1701.28,894.456),(-525.738,1618.01,1051.5)]
  Start = (552.796,1701.28,894.456)
  Subdivisions = 0
FEATURE [Part::Part2DObjectPython] Line071  # Draft 2D object (typed FeaturePython)
  ChamferSize = 0
  Closed = false
  End = (324.929,1000.03,1701.28)
  FilletRadius = 0
  Length = 1236.02
  MakeFace = true
  Points = (2) [(-525.738,1618.01,1051.5),(324.929,1000.03,1701.28)]
  Start = (-525.738,1618.01,1051.5)
  Subdivisions = 0
FEATURE [Part::Part2DObjectPython] Line072  # Draft 2D object (typed FeaturePython)
  ChamferSize = 0
  Closed = false
  End = (3.6e-11,2000,0)
  FilletRadius = 0
  Length = 1236.11
  MakeFace = true
  Points = (2) [(-525.738,1618.01,1051.5),(3.56977e-11,2000,0)]
  Start = (-525.738,1618.01,1051.5)
  Subdivisions = 0
FEATURE [Part::Part2DObjectPython] Line073  # Draft 2D object (typed FeaturePython)
  ChamferSize = 0
  Closed = false
  End = (552.796,1701.28,894.456)
  FilletRadius = 0
  Length = 1093.1
  MakeFace = true
  Points = (2) [(3.56977e-11,2000,0),(552.796,1701.28,894.456)]
  Start = (3.6e-11,2000,0)
  Subdivisions = 0
FEATURE [Part::Part2DObjectPython] Line074  # Draft 2D object (typed FeaturePython)
  ChamferSize = 0
  Closed = false
  End = (-525.738,1618.01,1051.5)
  FilletRadius = 0
  Length = 1093.08
  MakeFace = true
  Points = (2) [(552.796,1701.28,894.456),(-525.738,1618.01,1051.5)]
  Start = (552.796,1701.28,894.456)
  Subdivisions = 0
FEATURE [Part::Part2DObjectPython] Line075  # Draft 2D object (typed FeaturePython)
  ChamferSize = 0
  Closed = false
  End = (1175.6,1618.02,0)
  FilletRadius = 0
  Length = 1236.11
  MakeFace = true
  Points = (2) [(1376.39,999.957,1051.5),(1175.6,1618.02,0)]
  Start = (1376.39,999.957,1051.5)
  Subdivisions = 0
FEATURE [Part::Part2DObjectPython] Line076  # Draft 2D object (typed FeaturePython)
  ChamferSize = 0
  Closed = false
  End = (552.796,1701.28,894.456)
  FilletRadius = 0
  Length = 1093.1
  MakeFace = true
  Points = (2) [(1175.6,1618.02,0),(552.796,1701.28,894.456)]
  Start = (1175.6,1618.02,0)
  Subdivisions = 0
FEATURE [Part::Part2DObjectPython] Line077  # Draft 2D object (typed FeaturePython)
  ChamferSize = 0
  Closed = false
  End = (-3.6e-11,2000,0)
  FilletRadius = 0
  Length = 1236.1
  MakeFace = true
  Points = (2) [(1175.6,1618.02,0),(-3.5925e-11,2000,0)]
  Start = (1175.6,1618.02,0)
  Subdivisions = 0
FEATURE [Part::Part2DObjectPython] Line078  # Draft 2D object (typed FeaturePython)
  ChamferSize = 0
  Closed = false
  End = (1175.6,1618.02,0)
  FilletRadius = 0
  Length = 1236.1
  MakeFace = true
  Points = (2) [(1902.16,617.998,0),(1175.6,1618.02,0)]
  Start = (1902.16,617.998,0)
  Subdivisions = 0
FEATURE [Part::Part2DObjectPython] Line079  # Draft 2D object (typed FeaturePython)
  ChamferSize = 0
  Closed = false
  End = (1788.83,-9.65e-10,894.484)
  FilletRadius = 0
  Length = 1092.97
  MakeFace = true
  Points = (2) [(1051.49,1.3321e-09,1701.28),(1788.83,-9.64734e-10,894.484)]
  Start = (1051.49,1.332e-09,1701.28)
  Subdivisions = 0
FEATURE [Part::Part2DObjectPython] Line080  # Draft 2D object (typed FeaturePython)
  ChamferSize = 0
  Closed = false
  End = (1376.39,-999.957,1051.5)
  FilletRadius = 0
  Length = 1093.01
  MakeFace = true
  Points = (2) [(1788.83,-9.64734e-10,894.484),(1376.39,-999.957,1051.5)]
  Start = (1788.83,-9.65e-10,894.484)
  Subdivisions = 0
FEATURE [Part::Part2DObjectPython] Line081  # Draft 2D object (typed FeaturePython)
  ChamferSize = 0
  Closed = false
  End = (1788.83,-9.65e-10,894.484)
  FilletRadius = 0
  Length = 1093.01
  MakeFace = true
  Points = (2) [(1376.39,-999.957,1051.5),(1788.83,-9.64734e-10,894.484)]
  Start = (1376.39,-999.957,1051.5)
  Subdivisions = 0
FEATURE [Part::Part2DObjectPython] Line082  # Draft 2D object (typed FeaturePython)
  ChamferSize = 0
  Closed = false
  End = (1902.16,-617.998,0)
  FilletRadius = 0
  Length = 1093.1
  MakeFace = true
  Points = (2) [(1788.83,-9.64734e-10,894.484),(1902.16,-617.998,0)]
  Start = (1788.83,-9.65e-10,894.484)
  Subdivisions = 0
FEATURE [Part::Part2DObjectPython] Line083  # Draft 2D object (typed FeaturePython)
  ChamferSize = 0
  Closed = false
  End = (1902.16,617.998,0)
  FilletRadius = 0
  Length = 1093.1
  MakeFace = true
  Points = (2) [(1788.83,-9.64734e-10,894.484),(1902.16,617.998,0)]
  Start = (1788.83,-9.65e-10,894.484)
  Subdivisions = 0
FEATURE [Part::Part2DObjectPython] Line084  # Draft 2D object (typed FeaturePython)
  ChamferSize = 0
  Closed = false
  End = (1376.39,999.957,1051.5)
  FilletRadius = 0
  Length = 1093.01
  MakeFace = true
  Points = (2) [(1788.83,-9.64734e-10,894.484),(1376.39,999.957,1051.5)]
  Start = (1788.83,-9.65e-10,894.484)
  Subdivisions = 0
FEATURE [Part::Part2DObjectPython] Line085  # Draft 2D object (typed FeaturePython)
  ChamferSize = 0
  Closed = false
  End = (-525.738,1618.01,1051.5)
  FilletRadius = 0
  Length = 1236.01
  MakeFace = true
  Points = (2) [(-850.675,618.052,1701.28),(-525.738,1618.01,1051.5)]
  Start = (-850.675,618.052,1701.28)
  Subdivisions = 0
FEATURE [Part::Part2DObjectPython] Line086  # Draft 2D object (typed FeaturePython)
  ChamferSize = 0
  Closed = false
  End = (-1175.6,1618.02,0)
  FilletRadius = 0
  Length = 1236.11
  MakeFace = true
  Points = (2) [(-525.738,1618.01,1051.5),(-1175.6,1618.02,0)]
  Start = (-525.738,1618.01,1051.5)
  Subdivisions = 0
FEATURE [Part::Part2DObjectPython] Line087  # Draft 2D object (typed FeaturePython)
  ChamferSize = 0
  Closed = false
  End = (-1175.6,1618.02,0)
  FilletRadius = 0
  Length = 1236.1
  MakeFace = true
  Points = (2) [(3.56977e-11,2000,0),(-1175.6,1618.02,0)]
  Start = (3.6e-11,2000,0)
  Subdivisions = 0
FEATURE [Part::Part2DObjectPython] Line088  # Draft 2D object (typed FeaturePython)
  ChamferSize = 0
  Closed = false
  End = (-1701.28,-1.022e-09,1051.5)
  FilletRadius = 0
  Length = 1236.02
  MakeFace = true
  Points = (2) [(-850.675,618.052,1701.28),(-1701.28,-1.02242e-09,1051.5)]
  Start = (-850.675,618.052,1701.28)
  Subdivisions = 0
FEATURE [Part::Part2DObjectPython] Line089  # Draft 2D object (typed FeaturePython)
  ChamferSize = 0
  Closed = false
  End = (-1175.6,1618.02,0)
  FilletRadius = 0
  Length = 1236.1
  MakeFace = true
  Points = (2) [(-1902.16,617.998,0),(-1175.6,1618.02,0)]
  Start = (-1902.16,617.998,0)
  Subdivisions = 0
FEATURE [Part::Part2DObjectPython] Line090  # Draft 2D object (typed FeaturePython)
  ChamferSize = 0
  Closed = false
  End = (-1447.21,1051.46,894.426)
  FilletRadius = 0
  Length = 1093.05
  MakeFace = true
  Points = (2) [(-525.738,1618.01,1051.5),(-1447.21,1051.46,894.426)]
  Start = (-525.738,1618.01,1051.5)
  Subdivisions = 0
FEATURE [Part::Part2DObjectPython] Line091  # Draft 2D object (typed FeaturePython)
  ChamferSize = 0
  Closed = false
  End = (-1175.6,1618.02,0)
  FilletRadius = 0
  Length = 1093.05
  MakeFace = true
  Points = (2) [(-1447.21,1051.46,894.426),(-1175.6,1618.02,0)]
  Start = (-1447.21,1051.46,894.426)
  Subdivisions = 0
FEATURE [Part::Part2DObjectPython] Line092  # Draft 2D object (typed FeaturePython)
  ChamferSize = 0
  Closed = false
  End = (-1902.16,617.998,0)
  FilletRadius = 0
  Length = 1093.1
  MakeFace = true
  Points = (2) [(-1447.21,1051.46,894.426),(-1902.16,617.998,0)]
  Start = (-1447.21,1051.46,894.426)
  Subdivisions = 0
FEATURE [Part::Part2DObjectPython] Line093  # Draft 2D object (typed FeaturePython)
  ChamferSize = 0
  Closed = false
  End = (-1701.28,-1.022e-09,1051.5)
  FilletRadius = 0
  Length = 1093.07
  MakeFace = true
  Points = (2) [(-1447.21,1051.46,894.426),(-1701.28,-1.02242e-09,1051.5)]
  Start = (-1447.21,1051.46,894.426)
  Subdivisions = 0
FEATURE [Part::Part2DObjectPython] Line094  # Draft 2D object (typed FeaturePython)
  ChamferSize = 0
  Closed = false
  End = (-850.675,618.052,1701.28)
  FilletRadius = 0
  Length = 1093.03
  MakeFace = true
  Points = (2) [(-1447.21,1051.46,894.426),(-850.675,618.052,1701.28)]
  Start = (-1447.21,1051.46,894.426)
  Subdivisions = 0
FEATURE [Part::Part2DObjectPython] Line095  # Draft 2D object (typed FeaturePython)
  ChamferSize = 0
  Closed = false
  End = (-850.675,618.052,1701.28)
  FilletRadius = 0
  Length = 1236.1
  MakeFace = true
  Points = (2) [(324.929,1000.03,1701.28),(-850.675,618.052,1701.28)]
  Start = (324.929,1000.03,1701.28)
  Subdivisions = 0
FEATURE [Part::Part2DObjectPython] Line096  # Draft 2D object (typed FeaturePython)
  ChamferSize = 0
  Closed = false
  End = (-1902.16,617.998,0)
  FilletRadius = 0
  Length = 1236.09
  MakeFace = true
  Points = (2) [(-1701.28,-1.02242e-09,1051.5),(-1902.16,617.998,0)]
  Start = (-1701.28,-1.022e-09,1051.5)
  Subdivisions = 0
FEATURE [Part::Part2DObjectPython] Line097  # Draft 2D object (typed FeaturePython)
  ChamferSize = 0
  Closed = false
  End = (1175.6,-1618.02,0)
  FilletRadius = 0
  Length = 1236.11
  MakeFace = true
  Points = (2) [(1376.39,-999.957,1051.5),(1175.6,-1618.02,0)]
  Start = (1376.39,-999.957,1051.5)
  Subdivisions = 0
FEATURE [Part::Part2DObjectPython] Line098  # Draft 2D object (typed FeaturePython)
  ChamferSize = 0
  Closed = false
  End = (552.796,-1701.28,894.456)
  FilletRadius = 0
  Length = 1093.1
  MakeFace = true
  Points = (2) [(1175.6,-1618.02,0),(552.796,-1701.28,894.456)]
  Start = (1175.6,-1618.02,0)
  Subdivisions = 0
FEATURE [Part::Part2DObjectPython] Line099  # Draft 2D object (typed FeaturePython)
  ChamferSize = 0
  Closed = false
  End = (1376.39,-999.957,1051.5)
  FilletRadius = 0
  Length = 1093.08
  MakeFace = true
  Points = (2) [(552.796,-1701.28,894.456),(1376.39,-999.957,1051.5)]
  Start = (552.796,-1701.28,894.456)
  Subdivisions = 0
FEATURE [Part::Part2DObjectPython] Line100  # Draft 2D object (typed FeaturePython)
  ChamferSize = 0
  Closed = false
  End = (324.937,-1000.03,1701.28)
  FilletRadius = 0
  Length = 1093
  MakeFace = true
  Points = (2) [(552.796,-1701.28,894.456),(324.937,-1000.03,1701.28)]
  Start = (552.796,-1701.28,894.456)
  Subdivisions = 0
FEATURE [Part::Part2DObjectPython] Line101  # Draft 2D object (typed FeaturePython)
  ChamferSize = 0
  Closed = false
  End = (-525.738,-1618.01,1051.5)
  FilletRadius = 0
  Length = 1236.03
  MakeFace = true
  Points = (2) [(324.937,-1000.03,1701.28),(-525.738,-1618.01,1051.5)]
  Start = (324.937,-1000.03,1701.28)
  Subdivisions = 0
FEATURE [Part::Part2DObjectPython] Line102  # Draft 2D object (typed FeaturePython)
  ChamferSize = 0
  Closed = false
  End = (552.796,-1701.28,894.456)
  FilletRadius = 0
  Length = 1093.08
  MakeFace = true
  Points = (2) [(-525.738,-1618.01,1051.5),(552.796,-1701.28,894.456)]
  Start = (-525.738,-1618.01,1051.5)
  Subdivisions = 0
FEATURE [Part::Part2DObjectPython] Line103  # Draft 2D object (typed FeaturePython)
  ChamferSize = 0
  Closed = false
  End = (-3.6e-11,-2000,0)
  FilletRadius = 0
  Length = 1093.1
  MakeFace = true
  Points = (2) [(552.796,-1701.28,894.456),(-3.5925e-11,-2000,0)]
  Start = (552.796,-1701.28,894.456)
  Subdivisions = 0
FEATURE [Part::Part2DObjectPython] Line104  # Draft 2D object (typed FeaturePython)
  ChamferSize = 0
  Closed = false
  End = (1175.6,-1618.02,0)
  FilletRadius = 0
  Length = 1236.1
  MakeFace = true
  Points = (2) [(-3.5925e-11,-2000,0),(1175.6,-1618.02,0)]
  Start = (-3.6e-11,-2000,0)
  Subdivisions = 0
FEATURE [Part::Part2DObjectPython] Line105  # Draft 2D object (typed FeaturePython)
  ChamferSize = 0
  Closed = false
  End = (-525.738,-1618.01,1051.5)
  FilletRadius = 0
  Length = 1236.11
  MakeFace = true
  Points = (2) [(-3.5925e-11,-2000,0),(-525.738,-1618.01,1051.5)]
  Start = (-3.6e-11,-2000,0)
  Subdivisions = 0
FEATURE [Part::Part2DObjectPython] Line106  # Draft 2D object (typed FeaturePython)
  ChamferSize = 0
  Closed = false
  End = (-850.675,-618.052,1701.28)
  FilletRadius = 0
  Length = 1236.02
  MakeFace = true
  Points = (2) [(-1701.28,-1.02242e-09,1051.5),(-850.675,-618.052,1701.28)]
  Start = (-1701.28,-1.022e-09,1051.5)
  Subdivisions = 0
FEATURE [Part::Part2DObjectPython] Line107  # Draft 2D object (typed FeaturePython)
  ChamferSize = 0
  Closed = false
  End = (-1902.16,-617.998,0)
  FilletRadius = 0
  Length = 1236.09
  MakeFace = true
  Points = (2) [(-1701.28,-1.02242e-09,1051.5),(-1902.16,-617.998,0)]
  Start = (-1701.28,-1.022e-09,1051.5)
  Subdivisions = 0
FEATURE [Part::Part2DObjectPython] Line108  # Draft 2D object (typed FeaturePython)
  ChamferSize = 0
  Closed = false
  End = (-1902.16,617.998,0)
  FilletRadius = 0
  Length = 1236
  MakeFace = true
  Points = (2) [(-1902.16,-617.998,0),(-1902.16,617.998,0)]
  Start = (-1902.16,-617.998,0)
  Subdivisions = 0
FEATURE [Part::Part2DObjectPython] Line109  # Draft 2D object (typed FeaturePython)
  ChamferSize = 0
  Closed = false
  End = (-525.738,-1618.01,1051.5)
  FilletRadius = 0
  Length = 1236.01
  MakeFace = true
  Points = (2) [(-850.675,-618.052,1701.28),(-525.738,-1618.01,1051.5)]
  Start = (-850.675,-618.052,1701.28)
  Subdivisions = 0
FEATURE [Part::Part2DObjectPython] Line110  # Draft 2D object (typed FeaturePython)
  ChamferSize = 0
  Closed = false
  End = (-1175.6,-1618.02,0)
  FilletRadius = 0
  Length = 1236.11
  MakeFace = true
  Points = (2) [(-525.738,-1618.01,1051.5),(-1175.6,-1618.02,0)]
  Start = (-525.738,-1618.01,1051.5)
  Subdivisions = 0
FEATURE [Part::Part2DObjectPython] Line111  # Draft 2D object (typed FeaturePython)
  ChamferSize = 0
  Closed = false
  End = (-1902.16,-617.998,0)
  FilletRadius = 0
  Length = 1236.1
  MakeFace = true
  Points = (2) [(-1175.6,-1618.02,0),(-1902.16,-617.998,0)]
  Start = (-1175.6,-1618.02,0)
  Subdivisions = 0
FEATURE [Part::Part2DObjectPython] Line112  # Draft 2D object (typed FeaturePython)
  ChamferSize = 0
  Closed = false
  End = (-1447.19,-1051.45,894.481)
  FilletRadius = 0
  Length = 1093.15
  MakeFace = true
  Points = (2) [(-1902.16,-617.998,0),(-1447.19,-1051.45,894.481)]
  Start = (-1902.16,-617.998,0)
  Subdivisions = 0
FEATURE [Part::Part2DObjectPython] Line113  # Draft 2D object (typed FeaturePython)
  ChamferSize = 0
  Closed = false
  End = (-1701.28,-1.022e-09,1051.5)
  FilletRadius = 0
  Length = 1093.05
  MakeFace = true
  Points = (2) [(-1447.19,-1051.45,894.481),(-1701.28,-1.02242e-09,1051.5)]
  Start = (-1447.19,-1051.45,894.481)
  Subdivisions = 0
FEATURE [Part::Part2DObjectPython] Line114  # Draft 2D object (typed FeaturePython)
  ChamferSize = 0
  Closed = false
  End = (-850.675,-618.052,1701.28)
  FilletRadius = 0
  Length = 1092.97
  MakeFace = true
  Points = (2) [(-1447.19,-1051.45,894.481),(-850.675,-618.052,1701.28)]
  Start = (-1447.19,-1051.45,894.481)
  Subdivisions = 0
FEATURE [Part::Part2DObjectPython] Line115  # Draft 2D object (typed FeaturePython)
  ChamferSize = 0
  Closed = false
  End = (-525.738,-1618.01,1051.5)
  FilletRadius = 0
  Length = 1093.03
  MakeFace = true
  Points = (2) [(-1447.19,-1051.45,894.481),(-525.738,-1618.01,1051.5)]
  Start = (-1447.19,-1051.45,894.481)
  Subdivisions = 0
FEATURE [Part::Part2DObjectPython] Line116  # Draft 2D object (typed FeaturePython)
  ChamferSize = 0
  Closed = false
  End = (-1175.6,-1618.02,0)
  FilletRadius = 0
  Length = 1093.1
  MakeFace = true
  Points = (2) [(-1447.19,-1051.45,894.481),(-1175.6,-1618.02,0)]
  Start = (-1447.19,-1051.45,894.481)
  Subdivisions = 0
FEATURE [Part::Part2DObjectPython] Line117  # Draft 2D object (typed FeaturePython)
  ChamferSize = 0
  Closed = false
  End = (-3.6e-11,-2000,0)
  FilletRadius = 0
  Length = 1236.1
  MakeFace = true
  Points = (2) [(-1175.6,-1618.02,0),(-3.5925e-11,-2000,0)]
  Start = (-1175.6,-1618.02,0)
  Subdivisions = 0
FEATURE [Part::Part2DObjectPython] Line118  # Draft 2D object (typed FeaturePython)
  ChamferSize = 0
  Closed = false
  End = (-850.675,618.052,1701.28)
  FilletRadius = 0
  Length = 1093.1
  MakeFace = true
  Points = (2) [(-1.99876e-10,3.00061e-10,2000),(-850.675,618.052,1701.28)]
  Start = (-2e-10,3e-10,2000)
  Subdivisions = 0
FEATURE [Part::Part2DObjectPython] Line119  # Draft 2D object (typed FeaturePython)
  ChamferSize = 0
  Closed = false
  End = (-850.675,-618.052,1701.28)
  FilletRadius = 0
  Length = 1093.1
  MakeFace = true
  Points = (2) [(-1.99876e-10,3.00061e-10,2000),(-850.675,-618.052,1701.28)]
  Start = (-2e-10,3e-10,2000)
  Subdivisions = 0
FEATURE [Part::Part2DObjectPython] Line120  # Draft 2D object (typed FeaturePython)
  ChamferSize = 0
  Closed = false
  End = (324.937,-1000.03,1701.28)
  FilletRadius = 0
  Length = 1093.1
  MakeFace = true
  Points = (2) [(-1.99876e-10,3.00061e-10,2000),(324.937,-1000.03,1701.28)]
  Start = (-2e-10,3e-10,2000)
  Subdivisions = 0
FEATURE [Part::Part2DObjectPython] Line121  # Draft 2D object (typed FeaturePython)
  ChamferSize = 0
  Closed = false
  End = (1051.49,1.332e-09,1701.28)
  FilletRadius = 0
  Length = 1093.1
  MakeFace = true
  Points = (2) [(-1.99876e-10,3.00061e-10,2000),(1051.49,1.3321e-09,1701.28)]
  Start = (-2e-10,3e-10,2000)
  Subdivisions = 0
FEATURE [Part::Part2DObjectPython] Line122  # Draft 2D object (typed FeaturePython)
  ChamferSize = 0
  Closed = false
  End = (324.929,1000.03,1701.28)
  FilletRadius = 0
  Length = 1093.1
  MakeFace = true
  Points = (2) [(-1.99876e-10,3.00061e-10,2000),(324.929,1000.03,1701.28)]
  Start = (-2e-10,3e-10,2000)
  Subdivisions = 0
FEATURE [App::DocumentObjectGroup] Group013  label="Domo-alambrico"
  Group = -> [Line054,Line055,Line045,Line056,Line057,Line058,Line059,Line060,Line061,Line062,Line063,Line064,Line065,Line066,Line067,Line068,Line069,Line070,Line071,Line072,Line073,Line074,Line075,Line076,Line077,Line078,Line079,Line080,Line081,Line082,Line083,Line084,Line085,Line086,Line087,Line088,Line089,Line090,Line091,Line092,Line093,Line094,Line095,Line096,Line097,Line098,Line099,Line100,Line101,Line102,+20 more]
FEATURE [App::Annotation] Text  label="Texto-Material"
  LabelText = Material
  Position = (3227.54,1318.45,0)
FEATURE [App::FeaturePython] Dimension002  # Draft dimension (typed FeaturePython)
  Dimline = (-3.6e-11,-2000,0)
  Direction = (0,0,0)
  Distance = 4000
  End = (-3.6e-11,-2000,0)
  Normal = (0,0,1)
  Start = (-3.6e-11,2000,0)
FEATURE [App::FeaturePython] Dimension003  # Draft dimension (typed FeaturePython)
  Dimline = (-2e-10,3e-10,0)
  Direction = (0,0,0)
  Distance = 2000
  End = (-2e-10,3e-10,0)
  Normal = (0,-1,0)
  Start = (-2e-10,3e-10,2000)
FEATURE [App::FeaturePython] Dimension004  # Draft dimension (typed FeaturePython)
  Dimline = (2000,-600,0)
  Direction = (0,0,0)
  Distance = 1236
  End = (1902.16,-617.998,0)
  Normal = (0,0,1)
  Start = (1902.16,617.998,0)
FEATURE [App::FeaturePython] Dimension005  # Draft dimension (typed FeaturePython)
  Dimline = (1692.93,0,1177.36)
  Direction = (0,0,0)
  Distance = 1092.97
  End = (1788.83,-9.65e-10,894.484)
  Normal = (0,-1,0)
  Start = (1051.49,1.332e-09,1701.28)
FEATURE [App::DocumentObjectGroup] Group014  label="Dimensions"
  Group = -> [Dimension002,Dimension003,Dimension004,Dimension005]
FEATURE [Part::Feature] Cylinder079  label="Varilla-B-modif-039"
  Placement = pos=(3067.05,988.83,0) rot=(1,1.4e-05,1.4e-05;1.5708rad)
  shape: bbox 10.03 x 1189 x 10 mm, 3 faces (baked)
FEATURE [Part::Feature] Cylinder081  label="Cylinder078"
  Placement = pos=(2871.13,-200,5.93e-10) rot=(-1,0,0;1.5708rad)
  shape: bbox 10 x 1047 x 10 mm, 3 faces (baked)
FEATURE [App::Annotation] Text002  label="Texto-varillas"
  LabelText = Varillas
  Position = (2851.65,1075.67,0)
FEATURE [App::Annotation] Text006  label="Texto-varilla-B"
  LabelText = B
  Position = (3045.54,-293.166,0)
FEATURE [App::Annotation] Text007  label="Texto-varilla-A"
  LabelText = A
  Position = (2839.02,-294.635,0)
FEATURE [Part::Feature] Clone001171  label="Hub5-01-clave008"
  Placement = pos=(3486.66,751.241,0) rot=(0,0,-1;0.314151rad)
  shape: bbox 54.38 x 55.6 x 12.4 mm, 25 faces (baked)
FEATURE [Part::Feature] Clone001172  label="Hub-032"
  Placement = pos=(3822.07,752.602,-1e-12) rot=(0,0,1;0.523599rad)
  shape: bbox 53.16 x 55.6 x 12.4 mm, 28 faces (baked)
FEATURE [App::Annotation] Text008  label="Texto-Piezas-impresas"
  LabelText = Piezas impresas 3D
  Position = (3335.62,1068.59,0)
FEATURE [App::Annotation] Text009  label="Texto-conector-pentagonal"
  LabelText = Conector | pentagonal
  Position = (3357.25,917.695,0)
FEATURE [App::Annotation] Text010  label="Texto-conector-hexagonal"
  LabelText = Conector | Hexagonal
  Position = (3702.82,917.695,0)
FEATURE [Part::Feature] Clone001176  label="strutcap177"
  Placement = pos=(3662.75,464.083,20) rot=(1,0,0;3.14159rad)
  shape: bbox 20.3 x 20 x 30 mm, 19 faces (baked)
FEATURE [App::Annotation] Text012  label="Texto-varillas005"
  LabelText = Teton
  Position = (3595.02,530.248,0)
FEATURE [Part::Feature] Chamfer002  label="Tuerca-M3"
  Placement = pos=(3453.75,-347.288,0) rot=(1,0,0;1.5708rad)
  shape: bbox 6.35 x 6.35 x 2.4 mm, 29 faces (baked)
FEATURE [Part::Feature] Part__Feature002  label="Tornillo-M3"
  Placement = pos=(3442.59,-46.9489,3) rot=(0,-1,0;1.5708rad)
  shape: bbox 13 x 5.5 x 5.5 mm, 16 faces (baked)
FEATURE [App::Annotation] Text017  label="Texto-x30"
  LabelText = x30
  Position = (2840.67,-387.052,0)
FEATURE [App::Annotation] Text019  label="Texto-x35"
  LabelText = x35
  Position = (3032.11,-387.052,0)
FEATURE [App::Annotation] Text020
  LabelText = Tuercas M3
  Position = (3378.67,-274.428,0)
FEATURE [App::Annotation] Text021
  LabelText = Tornillos M3 x 10mm
  Position = (3372,13.5051,0)
FEATURE [App::Annotation] Text022  label="Texto-x6"
  LabelText = x6
  Position = (3441.07,635.345,0)
FEATURE [App::Annotation] Text023  label="Texto-x20"
  LabelText = x20
  Position = (3785.21,635.345,0)
FEATURE [App::Annotation] Text024  label="Texto-x037"
  LabelText = x160
  Position = (3595.42,372.947,0)
FEATURE [Part::Part2DObjectPython] Rectangle  # Draft 2D object (typed FeaturePython)
  ChamferSize = 0
  Columns = 1
  FilletRadius = 0
  Height = -869.038
  Length = 778.826
  MakeFace = false
  Placement = pos=(3282.79,1174.01,0) rot=(0,0,1;0rad)
  Rows = 1
FEATURE [App::Annotation] Text026  label="Texto-Piezas-impresas002"
  LabelText = Tornilleria
  Position = (3493.63,154.878,0)
FEATURE [Part::Part2DObjectPython] Rectangle003  # Draft 2D object (typed FeaturePython)
  ChamferSize = 0
  Columns = 1
  FilletRadius = 0
  Height = -237.557
  Length = 1305.06
  MakeFace = false
  Placement = pos=(2748.42,1457.07,0) rot=(0,0,1;0rad)
  Rows = 1
FEATURE [App::DocumentObjectGroup] Group017  label="Piezas-impresas"
  Group = -> [Clone001171,Clone001172,Clone001176,Text008,Text022,Text023,Text024,Rectangle,Text009,Text010,Text012]
FEATURE [App::Annotation] Text027  label="Texto-x130"
  LabelText = x130
  Position = (3503.66,-74.9347,0)
FEATURE [App::Annotation] Text028  label="Texto-x131"
  LabelText = x130
  Position = (3509.07,-372.19,0)
FEATURE [Part::Part2DObjectPython] Rectangle004  # Draft 2D object (typed FeaturePython)
  ChamferSize = 0
  Columns = 1
  FilletRadius = 0
  Height = -688.616
  Length = 787.849
  MakeFace = false
  Placement = pos=(3285.28,239.952,0) rot=(0,0,1;0rad)
  Rows = 1
FEATURE [App::DocumentObjectGroup] Group018  label="Tornilleria"
  Group = -> [Text026,Text020,Text021,Part__Feature002,Chamfer002,Text027,Text028,Rectangle004]
FEATURE [Part::Part2DObjectPython] Rectangle005  # Draft 2D object (typed FeaturePython)
  ChamferSize = 0
  Columns = 1
  FilletRadius = 0
  Height = -1623.39
  Length = 466.45
  MakeFace = false
  Placement = pos=(2751.78,1169.58,0) rot=(0,0,1;0rad)
  Rows = 1
FEATURE [App::DocumentObjectGroup] Group016  label="Varillas"
  Group = -> [Cylinder079,Cylinder081,Text002,Text006,Text007,Text017,Text019,Rectangle005]
FEATURE [App::DocumentObjectGroup] Group015  label="Materiales"
  Group = -> [Group016,Text,Group017,Group018,Rectangle003]
FEATURE [Part::Feature] Clone001177  label="strutcap178"
  Placement = pos=(-20,-1.7e-11,-9.7e-11) rot=(0.707107,0,0.707107;3.14159rad)
  shape: bbox 30 x 20 x 20.3 mm, 19 faces (baked)
FEATURE [Part::Feature] Part__Feature  label="Tornillo-M004"
  Placement = pos=(-5.55,-1.7e-11,29.9) rot=(0,0,1;0rad)
  shape: bbox 5.5 x 5.5 x 13 mm, 16 faces (baked)
FEATURE [Part::Feature] Chamfer  label="Tuerca-M004"
  Placement = pos=(9.45,-1.7e-11,6.96667) rot=(1,0,0;1.5708rad)
  shape: bbox 6.35 x 6.35 x 2.4 mm, 29 faces (baked)
FEATURE [Part::Feature] Cylinder082  label="Varilla-B-modif-040"
  Placement = pos=(16.0356,-0.0024909,5.5791e-06) rot=(0.57734,0.577355,0.577355;2.09441rad)
  shape: bbox 1189 x 10.03 x 10 mm, 3 faces (baked)
FEATURE [Part::Part2DObjectPython] Line124  # Draft 2D object (typed FeaturePython)
  ChamferSize = 0
  Closed = false
  End = (-5.55,-1.7e-11,6.56667)
  FilletRadius = 0
  Length = 2.8
  MakeFace = true
  Points = (2) [(-5.55,-1.70175e-11,9.36667),(-5.55,-1.70176e-11,6.56667)]
  Start = (-5.55,-1.7e-11,9.36667)
  Subdivisions = 0
  Support = -> Clone001177
FEATURE [Part::Part2DObjectPython] Line125  # Draft 2D object (typed FeaturePython)
  ChamferSize = 0
  Closed = false
  End = (6.7,-1.7e-11,8.16667)
  FilletRadius = 0
  Length = 12.2516
  MakeFace = true
  Points = (2) [(-5.55,-1.70176e-11,7.96667),(6.7,-1.70192e-11,8.16667)]
  Start = (-5.55,-1.7e-11,7.96667)
  Subdivisions = 0
FEATURE [Part::Part2DObjectPython] Line126  # Draft 2D object (typed FeaturePython)
  ChamferSize = 0
  Closed = false
  End = (-5.55,-1.7e-11,7.96667)
  FilletRadius = 0
  Length = 11.9333
  MakeFace = true
  Points = (2) [(-5.55,-1.70177e-11,19.9),(-5.55,-1.70176e-11,7.96667)]
  Start = (-5.55,-1.7e-11,19.9)
  Subdivisions = 0
FEATURE [Part::Part2DObjectPython] Line127  # Draft 2D object (typed FeaturePython)
  ChamferSize = 0
  Closed = false
  End = (-5.55,-1.7e-11,6.56667)
  FilletRadius = 0
  Length = 1.6
  MakeFace = true
  Points = (2) [(-5.55,-1.6,6.56667),(-5.55,-1.70176e-11,6.56667)]
  Start = (-5.55,-1.6,6.56667)
  Subdivisions = 0
FEATURE [Part::Part2DObjectPython] DWire046  # Draft 2D object (typed FeaturePython)
  ChamferSize = 0
  Closed = true
  End = (-5.55,-1.7e-11,9.36667)
  FilletRadius = 0
  Length = 7.6249
  MakeFace = true
  Points = (3) [(-5.55,-1.6,6.56667),(-5.55,-1.70176e-11,6.56667),(-5.55,-1.70175e-11,9.36667)]
  Start = (-5.55,-1.6,6.56667)
  Subdivisions = 0
FEATURE [Part::Part2DObjectPython] Line128  # Draft 2D object (typed FeaturePython)
  ChamferSize = 0
  Closed = false
  End = (-5.55,-0.0024909,5.5791e-06)
  FilletRadius = 0
  Length = 21.5856
  MakeFace = true
  Points = (2) [(16.0356,-0.0024909,5.5791e-06),(-5.55,-0.0024909,5.5791e-06)]
  Start = (16.0356,-0.0024909,5.5791e-06)
  Subdivisions = 0
  Support = -> DWire046
FEATURE [App::DocumentObjectGroup] Group020  label="Despiece"
  Group = -> [Clone001177,Part__Feature,Chamfer,Cylinder082,Line124,Line125,Line126,Line127,DWire046,Line128]
FEATURE [Part::Feature] Clone001178  label="strutcap179"
  Placement = pos=(-20,31.6617,-9.7e-11) rot=(0.707107,0,0.707107;3.14159rad)
  shape: bbox 30 x 20 x 20.3 mm, 19 faces (baked)
FEATURE [Part::Feature] Part__Feature003  label="Tornillo-M005"
  Placement = pos=(-5.55,31.6617,11.9) rot=(0,0,1;0rad)
  shape: bbox 5.5 x 5.5 x 13 mm, 16 faces (baked)
FEATURE [Part::Feature] Chamfer003  label="Tuerca-M005"
  Placement = pos=(-5.55,31.6617,6.96667) rot=(1,0,0;1.5708rad)
  shape: bbox 6.35 x 6.35 x 2.4 mm, 29 faces (baked)
FEATURE [Part::Feature] Cylinder083  label="Varilla-B-modif-041"
  Placement = pos=(-20,31.6617,5.5791e-06) rot=(0.57734,0.577355,0.577355;2.09441rad)
  shape: bbox 1189 x 10.03 x 10 mm, 3 faces (baked)
FEATURE [App::DocumentObjectGroup] Group021  label="Ensamblaje"
  Group = -> [Clone001178,Part__Feature003,Chamfer003,Cylinder083]
FEATURE [App::DocumentObjectGroup] Group019  label="Ensamblaje-tetones"
  Group = -> [Group020,Group021]
